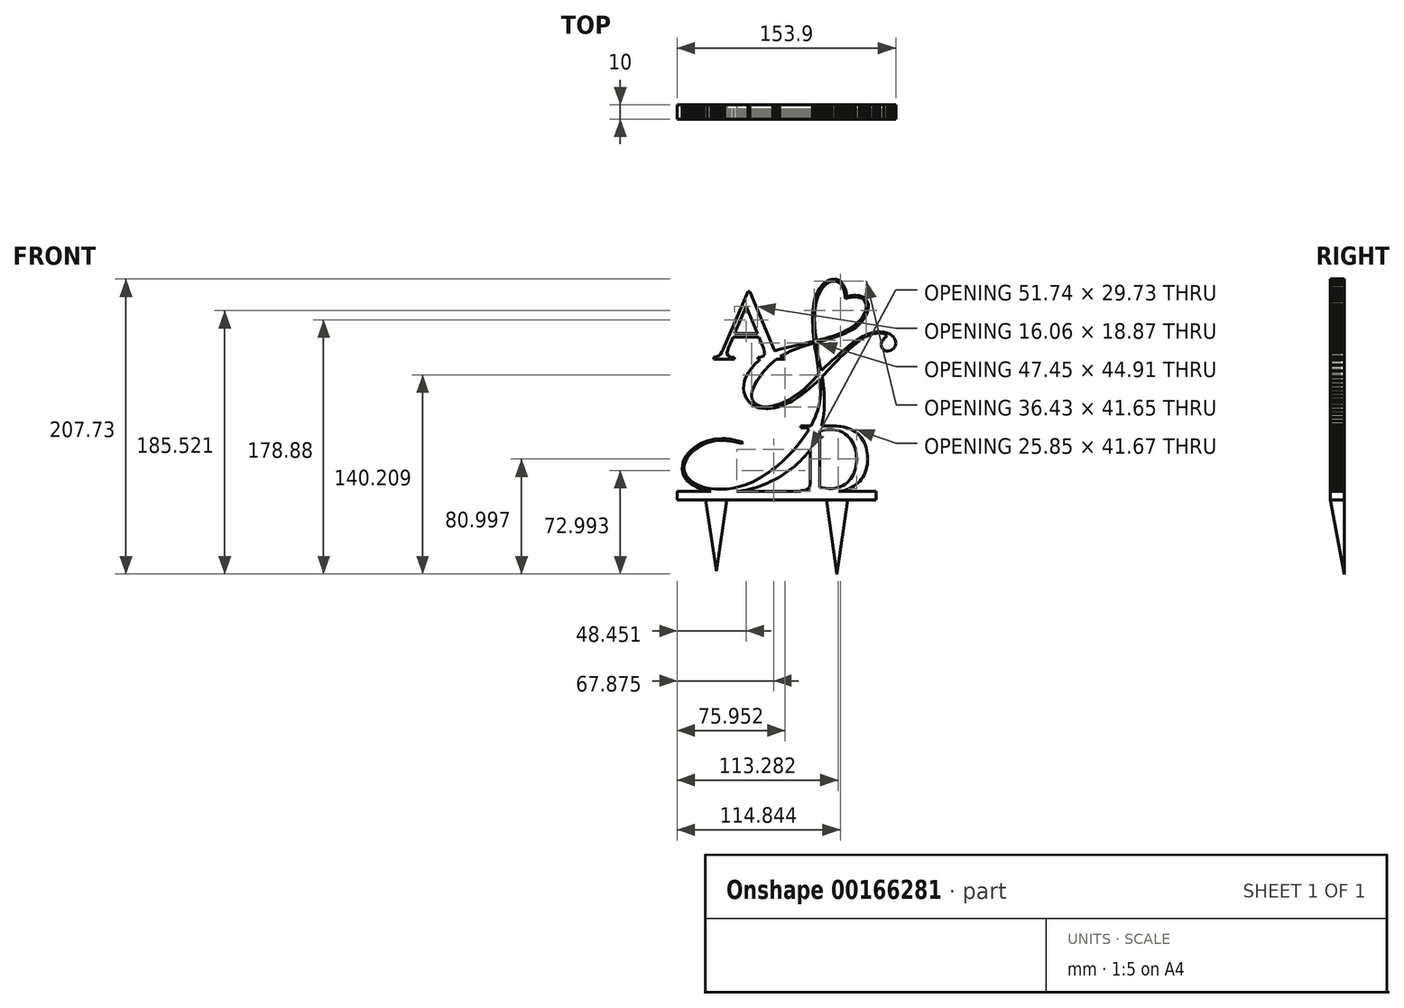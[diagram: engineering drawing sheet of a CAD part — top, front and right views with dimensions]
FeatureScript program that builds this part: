
annotation { "Feature Type Name" : "Feature", "Feature Type Description" : "" }
export const myFeature = defineFeature(function(context is Context, id is Id, definition is map)
    precondition{}
    {
        {
            var Q0;
            Q0=qCreatedBy(makeId("Front.planeOp"),FACE);
            var sketch = newSketch(context, id + "F0", { "sketchPlane" : qUnion([Q0])});
            skLineSegment(sketch, "E0", {"start": v(-55.06, -38.2) * mm, "end": v(-57.57, -38.87) * mm});
            skLineSegment(sketch, "E1", {"start": v(-57.57, -38.87) * mm, "end": v(-59.98, -39.75) * mm});
            skLineSegment(sketch, "E2", {"start": v(-59.98, -39.75) * mm, "end": v(-62.3, -40.8) * mm});
            skLineSegment(sketch, "E3", {"start": v(-62.3, -40.8) * mm, "end": v(-64.52, -42.07) * mm});
            skLineSegment(sketch, "E4", {"start": v(-64.52, -42.07) * mm, "end": v(-66.62, -43.52) * mm});
            skLineSegment(sketch, "E5", {"start": v(-66.62, -43.52) * mm, "end": v(-66.66, -43.54) * mm});
            skLineSegment(sketch, "E6", {"start": v(-66.66, -43.54) * mm, "end": v(-68.92, -45.38) * mm});
            skLineSegment(sketch, "E7", {"start": v(-68.92, -45.38) * mm, "end": v(-70.84, -47.32) * mm});
            skLineSegment(sketch, "E8", {"start": v(-70.84, -47.32) * mm, "end": v(-72.4, -49.38) * mm});
            skLineSegment(sketch, "E9", {"start": v(-72.4, -49.38) * mm, "end": v(-73.63, -51.52) * mm});
            skLineSegment(sketch, "E10", {"start": v(-73.63, -51.52) * mm, "end": v(-74.5, -53.78) * mm});
            skLineSegment(sketch, "E11", {"start": v(-74.5, -53.78) * mm, "end": v(-75.02, -56.15) * mm});
            skLineSegment(sketch, "E12", {"start": v(-75.02, -56.15) * mm, "end": v(-75.2, -58.6) * mm});
            skLineSegment(sketch, "E13", {"start": v(-75.2, -58.6) * mm, "end": v(-75, -60.71) * mm});
            skLineSegment(sketch, "E14", {"start": v(-75, -60.71) * mm, "end": v(-74.34, -62.91) * mm});
            skLineSegment(sketch, "E15", {"start": v(-74.34, -62.91) * mm, "end": v(-73.21, -64.97) * mm});
            skLineSegment(sketch, "E16", {"start": v(-73.21, -64.97) * mm, "end": v(-71.61, -66.9) * mm});
            skLineSegment(sketch, "E17", {"start": v(-71.61, -66.9) * mm, "end": v(-69.54, -68.71) * mm});
            skLineSegment(sketch, "E18", {"start": v(-69.54, -68.71) * mm, "end": v(-67, -70.37) * mm});
            skLineSegment(sketch, "E19", {"start": v(-67, -70.37) * mm, "end": v(-65.02, -71.44) * mm});
            skLineSegment(sketch, "E20", {"start": v(-65.02, -71.44) * mm, "end": v(-62.8, -72.42) * mm});
            skLineSegment(sketch, "E21", {"start": v(-62.8, -72.42) * mm, "end": v(-60.47, -73.23) * mm});
            skLineSegment(sketch, "E22", {"start": v(-60.47, -73.23) * mm, "end": v(-48.47, -72.93) * mm});
            skLineSegment(sketch, "E23", {"start": v(-48.47, -72.93) * mm, "end": v(-49.11, -72.93) * mm});
            skLineSegment(sketch, "E24", {"start": v(-49.11, -72.93) * mm, "end": v(-52.09, -72.82) * mm});
            skLineSegment(sketch, "E25", {"start": v(-52.09, -72.82) * mm, "end": v(-54.91, -72.54) * mm});
            skLineSegment(sketch, "E26", {"start": v(-54.91, -72.54) * mm, "end": v(-57.59, -72.08) * mm});
            skLineSegment(sketch, "E27", {"start": v(-57.59, -72.08) * mm, "end": v(-60.1, -71.46) * mm});
            skLineSegment(sketch, "E28", {"start": v(-60.1, -71.46) * mm, "end": v(-62.48, -70.67) * mm});
            skLineSegment(sketch, "E29", {"start": v(-62.48, -70.67) * mm, "end": v(-64.69, -69.71) * mm});
            skLineSegment(sketch, "E30", {"start": v(-64.69, -69.71) * mm, "end": v(-66.76, -68.58) * mm});
            skLineSegment(sketch, "E31", {"start": v(-66.76, -68.58) * mm, "end": v(-67.19, -68.32) * mm});
            skLineSegment(sketch, "E32", {"start": v(-67.19, -68.32) * mm, "end": v(-69.62, -66.55) * mm});
            skLineSegment(sketch, "E33", {"start": v(-69.62, -66.55) * mm, "end": v(-71.5, -64.65) * mm});
            skLineSegment(sketch, "E34", {"start": v(-71.5, -64.65) * mm, "end": v(-72.84, -62.63) * mm});
            skLineSegment(sketch, "E35", {"start": v(-72.84, -62.63) * mm, "end": v(-73.65, -60.5) * mm});
            skLineSegment(sketch, "E36", {"start": v(-73.65, -60.5) * mm, "end": v(-73.91, -58.23) * mm});
            skLineSegment(sketch, "E37", {"start": v(-73.91, -58.23) * mm, "end": v(-73.9, -57.47) * mm});
            skLineSegment(sketch, "E38", {"start": v(-73.9, -57.47) * mm, "end": v(-73.55, -55.21) * mm});
            skLineSegment(sketch, "E39", {"start": v(-73.55, -55.21) * mm, "end": v(-72.82, -53) * mm});
            skLineSegment(sketch, "E40", {"start": v(-72.82, -53) * mm, "end": v(-71.69, -50.84) * mm});
            skLineSegment(sketch, "E41", {"start": v(-71.69, -50.84) * mm, "end": v(-70.15, -48.74) * mm});
            skLineSegment(sketch, "E42", {"start": v(-70.15, -48.74) * mm, "end": v(-68.2, -46.66) * mm});
            skLineSegment(sketch, "E43", {"start": v(-68.2, -46.66) * mm, "end": v(-65.85, -44.67) * mm});
            skLineSegment(sketch, "E44", {"start": v(-65.85, -44.67) * mm, "end": v(-64.23, -43.52) * mm});
            skLineSegment(sketch, "E45", {"start": v(-64.23, -43.52) * mm, "end": v(-62.05, -42.18) * mm});
            skLineSegment(sketch, "E46", {"start": v(-62.05, -42.18) * mm, "end": v(-59.75, -41.07) * mm});
            skLineSegment(sketch, "E47", {"start": v(-59.75, -41.07) * mm, "end": v(-57.36, -40.15) * mm});
            skLineSegment(sketch, "E48", {"start": v(-57.36, -40.15) * mm, "end": v(-54.86, -39.43) * mm});
            skLineSegment(sketch, "E49", {"start": v(-54.86, -39.43) * mm, "end": v(-52.28, -38.93) * mm});
            skLineSegment(sketch, "E50", {"start": v(-52.28, -38.93) * mm, "end": v(-49.58, -38.63) * mm});
            skLineSegment(sketch, "E51", {"start": v(-49.58, -38.63) * mm, "end": v(-46.8, -38.53) * mm});
            skLineSegment(sketch, "E52", {"start": v(-46.8, -38.53) * mm, "end": v(-55.06, -38.2) * mm});
            skLineSegment(sketch, "E53", {"start": v(-46.55, -37.25) * mm, "end": v(-46.97, -37.25) * mm});
            skLineSegment(sketch, "E54", {"start": v(-46.97, -37.25) * mm, "end": v(-49.77, -37.38) * mm});
            skLineSegment(sketch, "E55", {"start": v(-49.77, -37.38) * mm, "end": v(-52.47, -37.68) * mm});
            skLineSegment(sketch, "E56", {"start": v(-52.47, -37.68) * mm, "end": v(-55.06, -38.2) * mm});
            skLineSegment(sketch, "E57", {"start": v(-55.06, -38.2) * mm, "end": v(-46.8, -38.53) * mm});
            skLineSegment(sketch, "E58", {"start": v(-46.8, -38.53) * mm, "end": v(-46.04, -38.53) * mm});
            skLineSegment(sketch, "E59", {"start": v(-46.04, -38.53) * mm, "end": v(-43.6, -38.66) * mm});
            skLineSegment(sketch, "E60", {"start": v(-43.6, -38.66) * mm, "end": v(-41.07, -38.96) * mm});
            skLineSegment(sketch, "E61", {"start": v(-41.07, -38.96) * mm, "end": v(-38.44, -39.43) * mm});
            skLineSegment(sketch, "E62", {"start": v(-38.44, -39.43) * mm, "end": v(-35.7, -40.06) * mm});
            skLineSegment(sketch, "E63", {"start": v(-35.7, -40.06) * mm, "end": v(-32.87, -40.83) * mm});
            skLineSegment(sketch, "E64", {"start": v(-32.87, -40.83) * mm, "end": v(-32.49, -39.94) * mm});
            skLineSegment(sketch, "E65", {"start": v(-32.49, -39.94) * mm, "end": v(-33.6, -39.55) * mm});
            skLineSegment(sketch, "E66", {"start": v(-33.6, -39.55) * mm, "end": v(-36.25, -38.72) * mm});
            skLineSegment(sketch, "E67", {"start": v(-36.25, -38.72) * mm, "end": v(-38.9, -38.08) * mm});
            skLineSegment(sketch, "E68", {"start": v(-38.9, -38.08) * mm, "end": v(-41.47, -37.6) * mm});
            skLineSegment(sketch, "E69", {"start": v(-41.47, -37.6) * mm, "end": v(-44.03, -37.34) * mm});
            skLineSegment(sketch, "E70", {"start": v(-44.03, -37.34) * mm, "end": v(-46.55, -37.25) * mm});
            skLineSegment(sketch, "E71", {"start": v(17.95, 5.17) * mm, "end": v(16.13, 3.12) * mm});
            skLineSegment(sketch, "E72", {"start": v(16.13, 3.12) * mm, "end": v(14.24, 1.14) * mm});
            skLineSegment(sketch, "E73", {"start": v(14.24, 1.14) * mm, "end": v(12.34, -0.72) * mm});
            skLineSegment(sketch, "E74", {"start": v(12.34, -0.72) * mm, "end": v(10.38, -2.47) * mm});
            skLineSegment(sketch, "E75", {"start": v(10.38, -2.47) * mm, "end": v(8.39, -4.13) * mm});
            skLineSegment(sketch, "E76", {"start": v(8.39, -4.13) * mm, "end": v(6.35, -5.68) * mm});
            skLineSegment(sketch, "E77", {"start": v(6.35, -5.68) * mm, "end": v(4.28, -7.13) * mm});
            skLineSegment(sketch, "E78", {"start": v(4.28, -7.13) * mm, "end": v(2.17, -8.46) * mm});
            skLineSegment(sketch, "E79", {"start": v(2.17, -8.46) * mm, "end": v(0.5, -9.46) * mm});
            skLineSegment(sketch, "E80", {"start": v(0.5, -9.46) * mm, "end": v(-2.14, -10.9) * mm});
            skLineSegment(sketch, "E81", {"start": v(-2.14, -10.9) * mm, "end": v(-4.72, -12.11) * mm});
            skLineSegment(sketch, "E82", {"start": v(-4.72, -12.11) * mm, "end": v(-7.24, -13.1) * mm});
            skLineSegment(sketch, "E83", {"start": v(-7.24, -13.1) * mm, "end": v(-9.69, -13.87) * mm});
            skLineSegment(sketch, "E84", {"start": v(-9.69, -13.87) * mm, "end": v(-12.06, -14.43) * mm});
            skLineSegment(sketch, "E85", {"start": v(-12.06, -14.43) * mm, "end": v(-14.38, -14.75) * mm});
            skLineSegment(sketch, "E86", {"start": v(-14.38, -14.75) * mm, "end": v(-16.63, -14.86) * mm});
            skLineSegment(sketch, "E87", {"start": v(-16.63, -14.86) * mm, "end": v(-7.65, -15.03) * mm});
            skLineSegment(sketch, "E88", {"start": v(-7.65, -15.03) * mm, "end": v(-5.11, -14.22) * mm});
            skLineSegment(sketch, "E89", {"start": v(-5.11, -14.22) * mm, "end": v(-2.51, -13.19) * mm});
            skLineSegment(sketch, "E90", {"start": v(-2.51, -13.19) * mm, "end": v(0.12, -11.93) * mm});
            skLineSegment(sketch, "E91", {"start": v(0.12, -11.93) * mm, "end": v(0.61, -11.68) * mm});
            skLineSegment(sketch, "E92", {"start": v(0.61, -11.68) * mm, "end": v(2.29, -10.76) * mm});
            skLineSegment(sketch, "E93", {"start": v(2.29, -10.76) * mm, "end": v(4.06, -9.67) * mm});
            skLineSegment(sketch, "E94", {"start": v(4.06, -9.67) * mm, "end": v(5.92, -8.42) * mm});
            skLineSegment(sketch, "E95", {"start": v(5.92, -8.42) * mm, "end": v(7.9, -7.03) * mm});
            skLineSegment(sketch, "E96", {"start": v(7.9, -7.03) * mm, "end": v(9.97, -5.47) * mm});
            skLineSegment(sketch, "E97", {"start": v(9.97, -5.47) * mm, "end": v(12.15, -3.75) * mm});
            skLineSegment(sketch, "E98", {"start": v(12.15, -3.75) * mm, "end": v(14.43, -1.87) * mm});
            skLineSegment(sketch, "E99", {"start": v(14.43, -1.87) * mm, "end": v(16.8, 0.16) * mm});
            skLineSegment(sketch, "E100", {"start": v(16.8, 0.16) * mm, "end": v(19.29, 2.35) * mm});
            skLineSegment(sketch, "E101", {"start": v(19.29, 2.35) * mm, "end": v(21.87, 4.7) * mm});
            skLineSegment(sketch, "E102", {"start": v(21.87, 4.7) * mm, "end": v(17.95, 5.17) * mm});
            skLineSegment(sketch, "E103", {"start": v(19.69, 30.42) * mm, "end": v(17.9, 30.04) * mm});
            skLineSegment(sketch, "E104", {"start": v(17.9, 30.04) * mm, "end": v(18.03, 27.09) * mm});
            skLineSegment(sketch, "E105", {"start": v(18.03, 27.09) * mm, "end": v(18.18, 26.52) * mm});
            skLineSegment(sketch, "E106", {"start": v(18.18, 26.52) * mm, "end": v(18.63, 24.24) * mm});
            skLineSegment(sketch, "E107", {"start": v(18.63, 24.24) * mm, "end": v(19.3, 20.3) * mm});
            skLineSegment(sketch, "E108", {"start": v(19.3, 20.3) * mm, "end": v(20.97, 8.94) * mm});
            skLineSegment(sketch, "E109", {"start": v(20.97, 8.94) * mm, "end": v(19.74, 7.35) * mm});
            skLineSegment(sketch, "E110", {"start": v(19.74, 7.35) * mm, "end": v(17.95, 5.17) * mm});
            skLineSegment(sketch, "E111", {"start": v(17.95, 5.17) * mm, "end": v(21.87, 4.7) * mm});
            skLineSegment(sketch, "E112", {"start": v(21.87, 4.7) * mm, "end": v(22.1, 2.57) * mm});
            skLineSegment(sketch, "E113", {"start": v(22.1, 2.57) * mm, "end": v(22.3, -0.16) * mm});
            skLineSegment(sketch, "E114", {"start": v(22.3, -0.16) * mm, "end": v(22.38, -2.46) * mm});
            skLineSegment(sketch, "E115", {"start": v(22.38, -2.46) * mm, "end": v(22.34, -4.06) * mm});
            skLineSegment(sketch, "E116", {"start": v(22.34, -4.06) * mm, "end": v(22.23, -6.35) * mm});
            skLineSegment(sketch, "E117", {"start": v(22.23, -6.35) * mm, "end": v(21.98, -8.65) * mm});
            skLineSegment(sketch, "E118", {"start": v(21.98, -8.65) * mm, "end": v(21.62, -10.93) * mm});
            skLineSegment(sketch, "E119", {"start": v(21.62, -10.93) * mm, "end": v(21.17, -13.23) * mm});
            skLineSegment(sketch, "E120", {"start": v(21.17, -13.23) * mm, "end": v(20.6, -15.5) * mm});
            skLineSegment(sketch, "E121", {"start": v(20.6, -15.5) * mm, "end": v(19.93, -17.8) * mm});
            skLineSegment(sketch, "E122", {"start": v(19.93, -17.8) * mm, "end": v(19.16, -20.08) * mm});
            skLineSegment(sketch, "E123", {"start": v(19.16, -20.08) * mm, "end": v(18.27, -22.36) * mm});
            skLineSegment(sketch, "E124", {"start": v(18.27, -22.36) * mm, "end": v(17.28, -24.64) * mm});
            skLineSegment(sketch, "E125", {"start": v(17.28, -24.64) * mm, "end": v(16.16, -26.91) * mm});
            skLineSegment(sketch, "E126", {"start": v(16.16, -26.91) * mm, "end": v(14.94, -29.2) * mm});
            skLineSegment(sketch, "E127", {"start": v(14.94, -29.2) * mm, "end": v(13.62, -31.45) * mm});
            skLineSegment(sketch, "E128", {"start": v(13.62, -31.45) * mm, "end": v(12.2, -33.73) * mm});
            skLineSegment(sketch, "E129", {"start": v(12.2, -33.73) * mm, "end": v(10.65, -35.99) * mm});
            skLineSegment(sketch, "E130", {"start": v(10.65, -35.99) * mm, "end": v(9, -38.25) * mm});
            skLineSegment(sketch, "E131", {"start": v(9, -38.25) * mm, "end": v(7.22, -40.5) * mm});
            skLineSegment(sketch, "E132", {"start": v(7.22, -40.5) * mm, "end": v(5.36, -42.77) * mm});
            skLineSegment(sketch, "E133", {"start": v(5.36, -42.77) * mm, "end": v(3.38, -45.03) * mm});
            skLineSegment(sketch, "E134", {"start": v(3.38, -45.03) * mm, "end": v(1.29, -47.29) * mm});
            skLineSegment(sketch, "E135", {"start": v(1.29, -47.29) * mm, "end": v(-0.9, -49.53) * mm});
            skLineSegment(sketch, "E136", {"start": v(-0.9, -49.53) * mm, "end": v(-2.9, -51.5) * mm});
            skLineSegment(sketch, "E137", {"start": v(-2.9, -51.5) * mm, "end": v(-5.17, -53.6) * mm});
            skLineSegment(sketch, "E138", {"start": v(-5.17, -53.6) * mm, "end": v(-7.4, -55.57) * mm});
            skLineSegment(sketch, "E139", {"start": v(-7.4, -55.57) * mm, "end": v(-9.67, -57.45) * mm});
            skLineSegment(sketch, "E140", {"start": v(-9.67, -57.45) * mm, "end": v(-11.9, -59.22) * mm});
            skLineSegment(sketch, "E141", {"start": v(-11.9, -59.22) * mm, "end": v(-14.17, -60.88) * mm});
            skLineSegment(sketch, "E142", {"start": v(-14.17, -60.88) * mm, "end": v(-16.43, -62.42) * mm});
            skLineSegment(sketch, "E143", {"start": v(-16.43, -62.42) * mm, "end": v(-18.7, -63.87) * mm});
            skLineSegment(sketch, "E144", {"start": v(-18.7, -63.87) * mm, "end": v(-20.97, -65.21) * mm});
            skLineSegment(sketch, "E145", {"start": v(-20.97, -65.21) * mm, "end": v(-23.24, -66.45) * mm});
            skLineSegment(sketch, "E146", {"start": v(-23.24, -66.45) * mm, "end": v(-25.52, -67.58) * mm});
            skLineSegment(sketch, "E147", {"start": v(-25.52, -67.58) * mm, "end": v(-27.8, -68.6) * mm});
            skLineSegment(sketch, "E148", {"start": v(-27.8, -68.6) * mm, "end": v(-30.08, -69.5) * mm});
            skLineSegment(sketch, "E149", {"start": v(-30.08, -69.5) * mm, "end": v(-32.36, -70.31) * mm});
            skLineSegment(sketch, "E150", {"start": v(-32.36, -70.31) * mm, "end": v(-34.65, -71) * mm});
            skLineSegment(sketch, "E151", {"start": v(-34.65, -71) * mm, "end": v(-36.95, -71.6) * mm});
            skLineSegment(sketch, "E152", {"start": v(-36.95, -71.6) * mm, "end": v(-39.25, -72.08) * mm});
            skLineSegment(sketch, "E153", {"start": v(-39.25, -72.08) * mm, "end": v(-41.54, -72.46) * mm});
            skLineSegment(sketch, "E154", {"start": v(-41.54, -72.46) * mm, "end": v(-43.84, -72.72) * mm});
            skLineSegment(sketch, "E155", {"start": v(-43.84, -72.72) * mm, "end": v(-46.16, -72.87) * mm});
            skLineSegment(sketch, "E156", {"start": v(-46.16, -72.87) * mm, "end": v(-48.47, -72.93) * mm});
            skLineSegment(sketch, "E157", {"start": v(-48.47, -72.93) * mm, "end": v(-60.47, -73.23) * mm});
            skLineSegment(sketch, "E158", {"start": v(-60.47, -73.23) * mm, "end": v(-58, -73.9) * mm});
            skLineSegment(sketch, "E159", {"start": v(-58, -73.9) * mm, "end": v(-55.38, -74.44) * mm});
            skLineSegment(sketch, "E160", {"start": v(-55.38, -74.44) * mm, "end": v(-52.65, -74.81) * mm});
            skLineSegment(sketch, "E161", {"start": v(-52.65, -74.81) * mm, "end": v(-49.8, -75.04) * mm});
            skLineSegment(sketch, "E162", {"start": v(-49.8, -75.04) * mm, "end": v(-46.8, -75.11) * mm});
            skLineSegment(sketch, "E163", {"start": v(-46.8, -75.11) * mm, "end": v(-45.56, -75.1) * mm});
            skLineSegment(sketch, "E164", {"start": v(-45.56, -75.1) * mm, "end": v(-42.9, -75.02) * mm});
            skLineSegment(sketch, "E165", {"start": v(-42.9, -75.02) * mm, "end": v(-40.26, -74.85) * mm});
            skLineSegment(sketch, "E166", {"start": v(-40.26, -74.85) * mm, "end": v(-37.65, -74.6) * mm});
            skLineSegment(sketch, "E167", {"start": v(-37.65, -74.6) * mm, "end": v(-35.07, -74.29) * mm});
            skLineSegment(sketch, "E168", {"start": v(-35.07, -74.29) * mm, "end": v(-32.5, -73.85) * mm});
            skLineSegment(sketch, "E169", {"start": v(-32.5, -73.85) * mm, "end": v(-29.97, -73.36) * mm});
            skLineSegment(sketch, "E170", {"start": v(-29.97, -73.36) * mm, "end": v(-27.46, -72.78) * mm});
            skLineSegment(sketch, "E171", {"start": v(-27.46, -72.78) * mm, "end": v(-24.98, -72.12) * mm});
            skLineSegment(sketch, "E172", {"start": v(-24.98, -72.12) * mm, "end": v(-22.53, -71.37) * mm});
            skLineSegment(sketch, "E173", {"start": v(-22.53, -71.37) * mm, "end": v(-20.1, -70.52) * mm});
            skLineSegment(sketch, "E174", {"start": v(-20.1, -70.52) * mm, "end": v(-17.69, -69.62) * mm});
            skLineSegment(sketch, "E175", {"start": v(-17.69, -69.62) * mm, "end": v(-15.32, -68.62) * mm});
            skLineSegment(sketch, "E176", {"start": v(-15.32, -68.62) * mm, "end": v(-12.94, -67.53) * mm});
            skLineSegment(sketch, "E177", {"start": v(-12.94, -67.53) * mm, "end": v(-10.63, -66.36) * mm});
            skLineSegment(sketch, "E178", {"start": v(-10.63, -66.36) * mm, "end": v(-8.31, -65.1) * mm});
            skLineSegment(sketch, "E179", {"start": v(-8.31, -65.1) * mm, "end": v(-6.05, -63.76) * mm});
            skLineSegment(sketch, "E180", {"start": v(-6.05, -63.76) * mm, "end": v(-3.8, -62.35) * mm});
            skLineSegment(sketch, "E181", {"start": v(-3.8, -62.35) * mm, "end": v(-1.57, -60.84) * mm});
            skLineSegment(sketch, "E182", {"start": v(-1.57, -60.84) * mm, "end": v(0.63, -59.26) * mm});
            skLineSegment(sketch, "E183", {"start": v(0.63, -59.26) * mm, "end": v(2.81, -57.59) * mm});
            skLineSegment(sketch, "E184", {"start": v(2.81, -57.59) * mm, "end": v(3.83, -56.76) * mm});
            skLineSegment(sketch, "E185", {"start": v(3.83, -56.76) * mm, "end": v(5.88, -55) * mm});
            skLineSegment(sketch, "E186", {"start": v(5.88, -55) * mm, "end": v(7.84, -53.18) * mm});
            skLineSegment(sketch, "E187", {"start": v(7.84, -53.18) * mm, "end": v(9.69, -51.32) * mm});
            skLineSegment(sketch, "E188", {"start": v(9.69, -51.32) * mm, "end": v(11.44, -49.4) * mm});
            skLineSegment(sketch, "E189", {"start": v(11.44, -49.4) * mm, "end": v(13.06, -47.44) * mm});
            skLineSegment(sketch, "E190", {"start": v(13.06, -47.44) * mm, "end": v(14.6, -45.4) * mm});
            skLineSegment(sketch, "E191", {"start": v(14.6, -45.4) * mm, "end": v(16.01, -43.33) * mm});
            skLineSegment(sketch, "E192", {"start": v(16.01, -43.33) * mm, "end": v(17.33, -41.2) * mm});
            skLineSegment(sketch, "E193", {"start": v(17.33, -41.2) * mm, "end": v(18.56, -39.04) * mm});
            skLineSegment(sketch, "E194", {"start": v(18.56, -39.04) * mm, "end": v(19.67, -36.8) * mm});
            skLineSegment(sketch, "E195", {"start": v(19.67, -36.8) * mm, "end": v(20.66, -34.52) * mm});
            skLineSegment(sketch, "E196", {"start": v(20.66, -34.52) * mm, "end": v(21.55, -32.19) * mm});
            skLineSegment(sketch, "E197", {"start": v(21.55, -32.19) * mm, "end": v(22.34, -29.81) * mm});
            skLineSegment(sketch, "E198", {"start": v(22.34, -29.81) * mm, "end": v(23.04, -27.37) * mm});
            skLineSegment(sketch, "E199", {"start": v(23.04, -27.37) * mm, "end": v(23.62, -24.88) * mm});
            skLineSegment(sketch, "E200", {"start": v(23.62, -24.88) * mm, "end": v(24.1, -22.34) * mm});
            skLineSegment(sketch, "E201", {"start": v(24.1, -22.34) * mm, "end": v(24.45, -19.76) * mm});
            skLineSegment(sketch, "E202", {"start": v(24.45, -19.76) * mm, "end": v(24.71, -17.1) * mm});
            skLineSegment(sketch, "E203", {"start": v(24.71, -17.1) * mm, "end": v(24.88, -14.41) * mm});
            skLineSegment(sketch, "E204", {"start": v(24.88, -14.41) * mm, "end": v(24.94, -11.66) * mm});
            skLineSegment(sketch, "E205", {"start": v(24.94, -11.66) * mm, "end": v(24.9, -9.87) * mm});
            skLineSegment(sketch, "E206", {"start": v(24.9, -9.87) * mm, "end": v(24.83, -7.48) * mm});
            skLineSegment(sketch, "E207", {"start": v(24.83, -7.48) * mm, "end": v(24.66, -4.96) * mm});
            skLineSegment(sketch, "E208", {"start": v(24.66, -4.96) * mm, "end": v(24.41, -2.32) * mm});
            skLineSegment(sketch, "E209", {"start": v(24.41, -2.32) * mm, "end": v(24.1, 0.44) * mm});
            skLineSegment(sketch, "E210", {"start": v(24.1, 0.44) * mm, "end": v(23.71, 3.34) * mm});
            skLineSegment(sketch, "E211", {"start": v(23.71, 3.34) * mm, "end": v(23.26, 6.37) * mm});
            skLineSegment(sketch, "E212", {"start": v(23.26, 6.37) * mm, "end": v(24.96, 8.26) * mm});
            skLineSegment(sketch, "E213", {"start": v(24.96, 8.26) * mm, "end": v(26.9, 10.4) * mm});
            skLineSegment(sketch, "E214", {"start": v(26.9, 10.4) * mm, "end": v(22.75, 10.6) * mm});
            skLineSegment(sketch, "E215", {"start": v(22.75, 10.6) * mm, "end": v(22.4, 12.08) * mm});
            skLineSegment(sketch, "E216", {"start": v(22.4, 12.08) * mm, "end": v(21.76, 14.85) * mm});
            skLineSegment(sketch, "E217", {"start": v(21.76, 14.85) * mm, "end": v(21.21, 17.58) * mm});
            skLineSegment(sketch, "E218", {"start": v(21.21, 17.58) * mm, "end": v(20.74, 20.23) * mm});
            skLineSegment(sketch, "E219", {"start": v(20.74, 20.23) * mm, "end": v(20.36, 22.85) * mm});
            skLineSegment(sketch, "E220", {"start": v(20.36, 22.85) * mm, "end": v(20.06, 25.43) * mm});
            skLineSegment(sketch, "E221", {"start": v(20.06, 25.43) * mm, "end": v(19.84, 27.95) * mm});
            skLineSegment(sketch, "E222", {"start": v(19.84, 27.95) * mm, "end": v(19.69, 30.42) * mm});
            skLineSegment(sketch, "E223", {"start": v(69.19, 37.2) * mm, "end": v(63.8, 37.07) * mm});
            skLineSegment(sketch, "E224", {"start": v(63.8, 37.07) * mm, "end": v(64.6, 37.03) * mm});
            skLineSegment(sketch, "E225", {"start": v(64.6, 37.03) * mm, "end": v(67.26, 36.43) * mm});
            skLineSegment(sketch, "E226", {"start": v(67.26, 36.43) * mm, "end": v(69.05, 35.14) * mm});
            skLineSegment(sketch, "E227", {"start": v(69.05, 35.14) * mm, "end": v(69.03, 35.05) * mm});
            skLineSegment(sketch, "E228", {"start": v(69.03, 35.05) * mm, "end": v(67.96, 34.19) * mm});
            skLineSegment(sketch, "E229", {"start": v(67.96, 34.19) * mm, "end": v(67, 33.22) * mm});
            skLineSegment(sketch, "E230", {"start": v(67, 33.22) * mm, "end": v(66.25, 32.44) * mm});
            skLineSegment(sketch, "E231", {"start": v(66.25, 32.44) * mm, "end": v(65.64, 31.58) * mm});
            skLineSegment(sketch, "E232", {"start": v(65.64, 31.58) * mm, "end": v(65.14, 30.44) * mm});
            skLineSegment(sketch, "E233", {"start": v(65.14, 30.44) * mm, "end": v(64.84, 29.14) * mm});
            skLineSegment(sketch, "E234", {"start": v(64.84, 29.14) * mm, "end": v(64.97, 27.9) * mm});
            skLineSegment(sketch, "E235", {"start": v(64.97, 27.9) * mm, "end": v(65.46, 26.72) * mm});
            skLineSegment(sketch, "E236", {"start": v(65.46, 26.72) * mm, "end": v(66.23, 25.7) * mm});
            skLineSegment(sketch, "E237", {"start": v(66.23, 25.7) * mm, "end": v(67.11, 24.98) * mm});
            skLineSegment(sketch, "E238", {"start": v(67.11, 24.98) * mm, "end": v(68.3, 24.5) * mm});
            skLineSegment(sketch, "E239", {"start": v(68.3, 24.5) * mm, "end": v(69.56, 24.28) * mm});
            skLineSegment(sketch, "E240", {"start": v(69.56, 24.28) * mm, "end": v(71.16, 24.56) * mm});
            skLineSegment(sketch, "E241", {"start": v(71.16, 24.56) * mm, "end": v(72.4, 25.23) * mm});
            skLineSegment(sketch, "E242", {"start": v(72.4, 25.23) * mm, "end": v(73.4, 26.07) * mm});
            skLineSegment(sketch, "E243", {"start": v(73.4, 26.07) * mm, "end": v(74.55, 27.5) * mm});
            skLineSegment(sketch, "E244", {"start": v(74.55, 27.5) * mm, "end": v(74.97, 28.68) * mm});
            skLineSegment(sketch, "E245", {"start": v(74.97, 28.68) * mm, "end": v(75.2, 29.91) * mm});
            skLineSegment(sketch, "E246", {"start": v(75.2, 29.91) * mm, "end": v(75.04, 31.23) * mm});
            skLineSegment(sketch, "E247", {"start": v(75.04, 31.23) * mm, "end": v(74.58, 32.37) * mm});
            skLineSegment(sketch, "E248", {"start": v(74.58, 32.37) * mm, "end": v(74.04, 33.45) * mm});
            skLineSegment(sketch, "E249", {"start": v(74.04, 33.45) * mm, "end": v(73.23, 34.63) * mm});
            skLineSegment(sketch, "E250", {"start": v(73.23, 34.63) * mm, "end": v(72.12, 35.54) * mm});
            skLineSegment(sketch, "E251", {"start": v(72.12, 35.54) * mm, "end": v(71.37, 36.09) * mm});
            skLineSegment(sketch, "E252", {"start": v(71.37, 36.09) * mm, "end": v(69.19, 37.2) * mm});
            skLineSegment(sketch, "E253", {"start": v(63.8, 38.1) * mm, "end": v(61.67, 37.95) * mm});
            skLineSegment(sketch, "E254", {"start": v(61.67, 37.95) * mm, "end": v(59.38, 37.54) * mm});
            skLineSegment(sketch, "E255", {"start": v(59.38, 37.54) * mm, "end": v(56.97, 36.82) * mm});
            skLineSegment(sketch, "E256", {"start": v(56.97, 36.82) * mm, "end": v(54.46, 35.82) * mm});
            skLineSegment(sketch, "E257", {"start": v(54.46, 35.82) * mm, "end": v(51.83, 34.54) * mm});
            skLineSegment(sketch, "E258", {"start": v(51.83, 34.54) * mm, "end": v(49.1, 32.98) * mm});
            skLineSegment(sketch, "E259", {"start": v(49.1, 32.98) * mm, "end": v(47.78, 32.13) * mm});
            skLineSegment(sketch, "E260", {"start": v(47.78, 32.13) * mm, "end": v(46.3, 31.13) * mm});
            skLineSegment(sketch, "E261", {"start": v(46.3, 31.13) * mm, "end": v(44.73, 29.99) * mm});
            skLineSegment(sketch, "E262", {"start": v(44.73, 29.99) * mm, "end": v(43.03, 28.69) * mm});
            skLineSegment(sketch, "E263", {"start": v(43.03, 28.69) * mm, "end": v(41.22, 27.26) * mm});
            skLineSegment(sketch, "E264", {"start": v(41.22, 27.26) * mm, "end": v(39.32, 25.67) * mm});
            skLineSegment(sketch, "E265", {"start": v(39.32, 25.67) * mm, "end": v(37.29, 23.96) * mm});
            skLineSegment(sketch, "E266", {"start": v(37.29, 23.96) * mm, "end": v(35.14, 22.1) * mm});
            skLineSegment(sketch, "E267", {"start": v(35.14, 22.1) * mm, "end": v(32.9, 20.08) * mm});
            skLineSegment(sketch, "E268", {"start": v(32.9, 20.08) * mm, "end": v(30.53, 17.92) * mm});
            skLineSegment(sketch, "E269", {"start": v(30.53, 17.92) * mm, "end": v(28.04, 15.62) * mm});
            skLineSegment(sketch, "E270", {"start": v(28.04, 15.62) * mm, "end": v(25.47, 13.17) * mm});
            skLineSegment(sketch, "E271", {"start": v(25.47, 13.17) * mm, "end": v(22.75, 10.6) * mm});
            skLineSegment(sketch, "E272", {"start": v(22.75, 10.6) * mm, "end": v(26.9, 10.4) * mm});
            skLineSegment(sketch, "E273", {"start": v(26.9, 10.4) * mm, "end": v(28.82, 12.48) * mm});
            skLineSegment(sketch, "E274", {"start": v(28.82, 12.48) * mm, "end": v(30.72, 14.49) * mm});
            skLineSegment(sketch, "E275", {"start": v(30.72, 14.49) * mm, "end": v(32.6, 16.43) * mm});
            skLineSegment(sketch, "E276", {"start": v(32.6, 16.43) * mm, "end": v(34.47, 18.31) * mm});
            skLineSegment(sketch, "E277", {"start": v(34.47, 18.31) * mm, "end": v(36.3, 20.12) * mm});
            skLineSegment(sketch, "E278", {"start": v(36.3, 20.12) * mm, "end": v(38.12, 21.87) * mm});
            skLineSegment(sketch, "E279", {"start": v(38.12, 21.87) * mm, "end": v(39.9, 23.57) * mm});
            skLineSegment(sketch, "E280", {"start": v(39.9, 23.57) * mm, "end": v(41.68, 25.17) * mm});
            skLineSegment(sketch, "E281", {"start": v(41.68, 25.17) * mm, "end": v(42.2, 25.64) * mm});
            skLineSegment(sketch, "E282", {"start": v(42.2, 25.64) * mm, "end": v(44.86, 27.91) * mm});
            skLineSegment(sketch, "E283", {"start": v(44.86, 27.91) * mm, "end": v(47.3, 29.91) * mm});
            skLineSegment(sketch, "E284", {"start": v(47.3, 29.91) * mm, "end": v(49.53, 31.62) * mm});
            skLineSegment(sketch, "E285", {"start": v(49.53, 31.62) * mm, "end": v(51.52, 33.04) * mm});
            skLineSegment(sketch, "E286", {"start": v(51.52, 33.04) * mm, "end": v(53.3, 34.17) * mm});
            skLineSegment(sketch, "E287", {"start": v(53.3, 34.17) * mm, "end": v(54.86, 35.01) * mm});
            skLineSegment(sketch, "E288", {"start": v(54.86, 35.01) * mm, "end": v(56.08, 35.56) * mm});
            skLineSegment(sketch, "E289", {"start": v(56.08, 35.56) * mm, "end": v(58.62, 36.4) * mm});
            skLineSegment(sketch, "E290", {"start": v(58.62, 36.4) * mm, "end": v(61.18, 36.9) * mm});
            skLineSegment(sketch, "E291", {"start": v(61.18, 36.9) * mm, "end": v(63.8, 37.07) * mm});
            skLineSegment(sketch, "E292", {"start": v(63.8, 37.07) * mm, "end": v(69.19, 37.2) * mm});
            skLineSegment(sketch, "E293", {"start": v(69.19, 37.2) * mm, "end": v(66.66, 37.87) * mm});
            skLineSegment(sketch, "E294", {"start": v(66.66, 37.87) * mm, "end": v(63.8, 38.1) * mm});
            skLineSegment(sketch, "E295", {"start": v(51.8, 62.58) * mm, "end": v(46.16, 62.39) * mm});
            skLineSegment(sketch, "E296", {"start": v(46.16, 62.39) * mm, "end": v(49.06, 62.14) * mm});
            skLineSegment(sketch, "E297", {"start": v(49.06, 62.14) * mm, "end": v(51.37, 61.37) * mm});
            skLineSegment(sketch, "E298", {"start": v(51.37, 61.37) * mm, "end": v(53.01, 60.05) * mm});
            skLineSegment(sketch, "E299", {"start": v(53.01, 60.05) * mm, "end": v(54, 58.23) * mm});
            skLineSegment(sketch, "E300", {"start": v(54, 58.23) * mm, "end": v(54.35, 55.87) * mm});
            skLineSegment(sketch, "E301", {"start": v(54.35, 55.87) * mm, "end": v(54.24, 54.35) * mm});
            skLineSegment(sketch, "E302", {"start": v(54.24, 54.35) * mm, "end": v(53.76, 52.2) * mm});
            skLineSegment(sketch, "E303", {"start": v(53.76, 52.2) * mm, "end": v(52.86, 50.1) * mm});
            skLineSegment(sketch, "E304", {"start": v(52.86, 50.1) * mm, "end": v(51.58, 48) * mm});
            skLineSegment(sketch, "E305", {"start": v(51.58, 48) * mm, "end": v(49.87, 45.95) * mm});
            skLineSegment(sketch, "E306", {"start": v(49.87, 45.95) * mm, "end": v(47.78, 43.94) * mm});
            skLineSegment(sketch, "E307", {"start": v(47.78, 43.94) * mm, "end": v(45.27, 41.92) * mm});
            skLineSegment(sketch, "E308", {"start": v(45.27, 41.92) * mm, "end": v(44.28, 41.25) * mm});
            skLineSegment(sketch, "E309", {"start": v(44.28, 41.25) * mm, "end": v(42.4, 40.04) * mm});
            skLineSegment(sketch, "E310", {"start": v(42.4, 40.04) * mm, "end": v(40.38, 38.91) * mm});
            skLineSegment(sketch, "E311", {"start": v(40.38, 38.91) * mm, "end": v(38.21, 37.84) * mm});
            skLineSegment(sketch, "E312", {"start": v(38.21, 37.84) * mm, "end": v(35.92, 36.84) * mm});
            skLineSegment(sketch, "E313", {"start": v(35.92, 36.84) * mm, "end": v(33.49, 35.88) * mm});
            skLineSegment(sketch, "E314", {"start": v(33.49, 35.88) * mm, "end": v(30.93, 35) * mm});
            skLineSegment(sketch, "E315", {"start": v(30.93, 35) * mm, "end": v(28.21, 34.18) * mm});
            skLineSegment(sketch, "E316", {"start": v(28.21, 34.18) * mm, "end": v(25.4, 33.41) * mm});
            skLineSegment(sketch, "E317", {"start": v(25.4, 33.41) * mm, "end": v(22.42, 32.72) * mm});
            skLineSegment(sketch, "E318", {"start": v(22.42, 32.72) * mm, "end": v(19.3, 32.08) * mm});
            skLineSegment(sketch, "E319", {"start": v(19.3, 32.08) * mm, "end": v(17.9, 31.57) * mm});
            skLineSegment(sketch, "E320", {"start": v(17.9, 31.57) * mm, "end": v(-6.66, 25.56) * mm});
            skLineSegment(sketch, "E321", {"start": v(-6.66, 25.56) * mm, "end": v(-8.54, 25.01) * mm});
            skLineSegment(sketch, "E322", {"start": v(-8.54, 25.01) * mm, "end": v(-10.93, 24.17) * mm});
            skLineSegment(sketch, "E323", {"start": v(-10.93, 24.17) * mm, "end": v(-13.26, 23.13) * mm});
            skLineSegment(sketch, "E324", {"start": v(-13.26, 23.13) * mm, "end": v(-15.54, 21.9) * mm});
            skLineSegment(sketch, "E325", {"start": v(-15.54, 21.9) * mm, "end": v(-17.75, 20.5) * mm});
            skLineSegment(sketch, "E326", {"start": v(-17.75, 20.5) * mm, "end": v(-19.91, 18.91) * mm});
            skLineSegment(sketch, "E327", {"start": v(-19.91, 18.91) * mm, "end": v(-22, 17.14) * mm});
            skLineSegment(sketch, "E328", {"start": v(-22, 17.14) * mm, "end": v(-24.05, 15.19) * mm});
            skLineSegment(sketch, "E329", {"start": v(-24.05, 15.19) * mm, "end": v(-24.88, 14.32) * mm});
            skLineSegment(sketch, "E330", {"start": v(-24.88, 14.32) * mm, "end": v(-26.76, 12.16) * mm});
            skLineSegment(sketch, "E331", {"start": v(-26.76, 12.16) * mm, "end": v(-28.37, 9.93) * mm});
            skLineSegment(sketch, "E332", {"start": v(-28.37, 9.93) * mm, "end": v(-29.66, 7.66) * mm});
            skLineSegment(sketch, "E333", {"start": v(-29.66, 7.66) * mm, "end": v(-30.66, 5.36) * mm});
            skLineSegment(sketch, "E334", {"start": v(-30.66, 5.36) * mm, "end": v(-31.4, 3) * mm});
            skLineSegment(sketch, "E335", {"start": v(-31.4, 3) * mm, "end": v(-31.83, 0.61) * mm});
            skLineSegment(sketch, "E336", {"start": v(-31.83, 0.61) * mm, "end": v(-31.98, -1.82) * mm});
            skLineSegment(sketch, "E337", {"start": v(-31.98, -1.82) * mm, "end": v(-31.96, -2.06) * mm});
            skLineSegment(sketch, "E338", {"start": v(-31.96, -2.06) * mm, "end": v(-31.68, -4.53) * mm});
            skLineSegment(sketch, "E339", {"start": v(-31.68, -4.53) * mm, "end": v(-30.93, -6.92) * mm});
            skLineSegment(sketch, "E340", {"start": v(-30.93, -6.92) * mm, "end": v(-29.7, -9.27) * mm});
            skLineSegment(sketch, "E341", {"start": v(-29.7, -9.27) * mm, "end": v(-28, -11.53) * mm});
            skLineSegment(sketch, "E342", {"start": v(-28, -11.53) * mm, "end": v(-27.52, -12.08) * mm});
            skLineSegment(sketch, "E343", {"start": v(-27.52, -12.08) * mm, "end": v(-25.77, -13.55) * mm});
            skLineSegment(sketch, "E344", {"start": v(-25.77, -13.55) * mm, "end": v(-23.68, -14.68) * mm});
            skLineSegment(sketch, "E345", {"start": v(-23.68, -14.68) * mm, "end": v(-21.27, -15.48) * mm});
            skLineSegment(sketch, "E346", {"start": v(-21.27, -15.48) * mm, "end": v(-18.54, -15.97) * mm});
            skLineSegment(sketch, "E347", {"start": v(-18.54, -15.97) * mm, "end": v(-15.47, -16.14) * mm});
            skLineSegment(sketch, "E348", {"start": v(-15.47, -16.14) * mm, "end": v(-15.1, -16.14) * mm});
            skLineSegment(sketch, "E349", {"start": v(-15.1, -16.14) * mm, "end": v(-12.64, -16) * mm});
            skLineSegment(sketch, "E350", {"start": v(-12.64, -16) * mm, "end": v(-10.18, -15.62) * mm});
            skLineSegment(sketch, "E351", {"start": v(-10.18, -15.62) * mm, "end": v(-7.65, -15.03) * mm});
            skLineSegment(sketch, "E352", {"start": v(-7.65, -15.03) * mm, "end": v(-16.63, -14.86) * mm});
            skLineSegment(sketch, "E353", {"start": v(-16.63, -14.86) * mm, "end": v(-19.3, -14.64) * mm});
            skLineSegment(sketch, "E354", {"start": v(-19.3, -14.64) * mm, "end": v(-21.76, -13.87) * mm});
            skLineSegment(sketch, "E355", {"start": v(-21.76, -13.87) * mm, "end": v(-23.79, -12.57) * mm});
            skLineSegment(sketch, "E356", {"start": v(-23.79, -12.57) * mm, "end": v(-24.75, -11.63) * mm});
            skLineSegment(sketch, "E357", {"start": v(-24.75, -11.63) * mm, "end": v(-26.05, -9.44) * mm});
            skLineSegment(sketch, "E358", {"start": v(-26.05, -9.44) * mm, "end": v(-26.48, -6.94) * mm});
            skLineSegment(sketch, "E359", {"start": v(-26.48, -6.94) * mm, "end": v(-26.39, -5.79) * mm});
            skLineSegment(sketch, "E360", {"start": v(-26.39, -5.79) * mm, "end": v(-25.95, -3.83) * mm});
            skLineSegment(sketch, "E361", {"start": v(-25.95, -3.83) * mm, "end": v(-25.15, -1.63) * mm});
            skLineSegment(sketch, "E362", {"start": v(-25.15, -1.63) * mm, "end": v(-23.96, 0.84) * mm});
            skLineSegment(sketch, "E363", {"start": v(-23.96, 0.84) * mm, "end": v(-22.4, 3.55) * mm});
            skLineSegment(sketch, "E364", {"start": v(-22.4, 3.55) * mm, "end": v(-20.46, 6.49) * mm});
            skLineSegment(sketch, "E365", {"start": v(-20.46, 6.49) * mm, "end": v(-19.76, 7.49) * mm});
            skLineSegment(sketch, "E366", {"start": v(-19.76, 7.49) * mm, "end": v(-18.08, 9.67) * mm});
            skLineSegment(sketch, "E367", {"start": v(-18.08, 9.67) * mm, "end": v(-16.33, 11.74) * mm});
            skLineSegment(sketch, "E368", {"start": v(-16.33, 11.74) * mm, "end": v(-14.5, 13.7) * mm});
            skLineSegment(sketch, "E369", {"start": v(-14.5, 13.7) * mm, "end": v(-12.6, 15.53) * mm});
            skLineSegment(sketch, "E370", {"start": v(-12.6, 15.53) * mm, "end": v(-10.65, 17.24) * mm});
            skLineSegment(sketch, "E371", {"start": v(-10.65, 17.24) * mm, "end": v(-8.63, 18.84) * mm});
            skLineSegment(sketch, "E372", {"start": v(-8.63, 18.84) * mm, "end": v(-6.52, 20.3) * mm});
            skLineSegment(sketch, "E373", {"start": v(-6.52, 20.3) * mm, "end": v(-5.02, 21.25) * mm});
            skLineSegment(sketch, "E374", {"start": v(-5.02, 21.25) * mm, "end": v(-3.2, 22.27) * mm});
            skLineSegment(sketch, "E375", {"start": v(-3.2, 22.27) * mm, "end": v(-1.18, 23.26) * mm});
            skLineSegment(sketch, "E376", {"start": v(-1.18, 23.26) * mm, "end": v(1, 24.26) * mm});
            skLineSegment(sketch, "E377", {"start": v(1, 24.26) * mm, "end": v(3.38, 25.26) * mm});
            skLineSegment(sketch, "E378", {"start": v(3.38, 25.26) * mm, "end": v(5.92, 26.24) * mm});
            skLineSegment(sketch, "E379", {"start": v(5.92, 26.24) * mm, "end": v(8.65, 27.2) * mm});
            skLineSegment(sketch, "E380", {"start": v(8.65, 27.2) * mm, "end": v(11.55, 28.16) * mm});
            skLineSegment(sketch, "E381", {"start": v(11.55, 28.16) * mm, "end": v(14.64, 29.1) * mm});
            skLineSegment(sketch, "E382", {"start": v(14.64, 29.1) * mm, "end": v(17.9, 30.04) * mm});
            skLineSegment(sketch, "E383", {"start": v(17.9, 30.04) * mm, "end": v(19.69, 30.42) * mm});
            skLineSegment(sketch, "E384", {"start": v(19.69, 30.42) * mm, "end": v(23.07, 31.3) * mm});
            skLineSegment(sketch, "E385", {"start": v(23.07, 31.3) * mm, "end": v(26.4, 32.25) * mm});
            skLineSegment(sketch, "E386", {"start": v(26.4, 32.25) * mm, "end": v(29.55, 33.2) * mm});
            skLineSegment(sketch, "E387", {"start": v(29.55, 33.2) * mm, "end": v(32.49, 34.17) * mm});
            skLineSegment(sketch, "E388", {"start": v(32.49, 34.17) * mm, "end": v(35.22, 35.14) * mm});
            skLineSegment(sketch, "E389", {"start": v(35.22, 35.14) * mm, "end": v(37.76, 36.14) * mm});
            skLineSegment(sketch, "E390", {"start": v(37.76, 36.14) * mm, "end": v(40.1, 37.16) * mm});
            skLineSegment(sketch, "E391", {"start": v(40.1, 37.16) * mm, "end": v(42.22, 38.2) * mm});
            skLineSegment(sketch, "E392", {"start": v(42.22, 38.2) * mm, "end": v(44.14, 39.23) * mm});
            skLineSegment(sketch, "E393", {"start": v(44.14, 39.23) * mm, "end": v(45.88, 40.28) * mm});
            skLineSegment(sketch, "E394", {"start": v(45.88, 40.28) * mm, "end": v(47.4, 41.36) * mm});
            skLineSegment(sketch, "E395", {"start": v(47.4, 41.36) * mm, "end": v(48.72, 42.43) * mm});
            skLineSegment(sketch, "E396", {"start": v(48.72, 42.43) * mm, "end": v(50.88, 44.62) * mm});
            skLineSegment(sketch, "E397", {"start": v(50.88, 44.62) * mm, "end": v(52.7, 46.8) * mm});
            skLineSegment(sketch, "E398", {"start": v(52.7, 46.8) * mm, "end": v(54.08, 49.02) * mm});
            skLineSegment(sketch, "E399", {"start": v(54.08, 49.02) * mm, "end": v(55.08, 51.24) * mm});
            skLineSegment(sketch, "E400", {"start": v(55.08, 51.24) * mm, "end": v(55.69, 53.48) * mm});
            skLineSegment(sketch, "E401", {"start": v(55.69, 53.48) * mm, "end": v(55.87, 55.74) * mm});
            skLineSegment(sketch, "E402", {"start": v(55.87, 55.74) * mm, "end": v(55.78, 57.1) * mm});
            skLineSegment(sketch, "E403", {"start": v(55.78, 57.1) * mm, "end": v(55, 59.53) * mm});
            skLineSegment(sketch, "E404", {"start": v(55, 59.53) * mm, "end": v(53.44, 61.5) * mm});
            skLineSegment(sketch, "E405", {"start": v(53.44, 61.5) * mm, "end": v(51.8, 62.58) * mm});
            skLineSegment(sketch, "E406", {"start": v(-27.69, 66.39) * mm, "end": v(-28.9, 66.39) * mm});
            skLineSegment(sketch, "E407", {"start": v(-28.9, 66.39) * mm, "end": v(-45.3, 27.96) * mm});
            skLineSegment(sketch, "E408", {"start": v(-45.3, 27.96) * mm, "end": v(-45.37, 27.77) * mm});
            skLineSegment(sketch, "E409", {"start": v(-45.37, 27.77) * mm, "end": v(-46.4, 25.53) * mm});
            skLineSegment(sketch, "E410", {"start": v(-46.4, 25.53) * mm, "end": v(-47.38, 23.7) * mm});
            skLineSegment(sketch, "E411", {"start": v(-47.38, 23.7) * mm, "end": v(-48.33, 22.27) * mm});
            skLineSegment(sketch, "E412", {"start": v(-48.33, 22.27) * mm, "end": v(-49.2, 21.26) * mm});
            skLineSegment(sketch, "E413", {"start": v(-49.2, 21.26) * mm, "end": v(-49.32, 21.14) * mm});
            skLineSegment(sketch, "E414", {"start": v(-49.32, 21.14) * mm, "end": v(-50.7, 20.46) * mm});
            skLineSegment(sketch, "E415", {"start": v(-50.7, 20.46) * mm, "end": v(-53, 19.92) * mm});
            skLineSegment(sketch, "E416", {"start": v(-53, 19.92) * mm, "end": v(-53, 18.64) * mm});
            skLineSegment(sketch, "E417", {"start": v(-53, 18.64) * mm, "end": v(-38.29, 18.64) * mm});
            skLineSegment(sketch, "E418", {"start": v(-38.29, 18.64) * mm, "end": v(-38.29, 19.92) * mm});
            skLineSegment(sketch, "E419", {"start": v(-38.29, 19.92) * mm, "end": v(-39.34, 20) * mm});
            skLineSegment(sketch, "E420", {"start": v(-39.34, 20) * mm, "end": v(-41.42, 20.33) * mm});
            skLineSegment(sketch, "E421", {"start": v(-41.42, 20.33) * mm, "end": v(-42.66, 20.92) * mm});
            skLineSegment(sketch, "E422", {"start": v(-42.66, 20.92) * mm, "end": v(-42.98, 21.2) * mm});
            skLineSegment(sketch, "E423", {"start": v(-42.98, 21.2) * mm, "end": v(-43.66, 22.84) * mm});
            skLineSegment(sketch, "E424", {"start": v(-43.66, 22.84) * mm, "end": v(-43.66, 23.12) * mm});
            skLineSegment(sketch, "E425", {"start": v(-43.66, 23.12) * mm, "end": v(-43.32, 24.76) * mm});
            skLineSegment(sketch, "E426", {"start": v(-43.32, 24.76) * mm, "end": v(-42.5, 26.87) * mm});
            skLineSegment(sketch, "E427", {"start": v(-42.5, 26.87) * mm, "end": v(-39.34, 34.25) * mm});
            skLineSegment(sketch, "E428", {"start": v(-39.34, 34.25) * mm, "end": v(-21.27, 34.25) * mm});
            skLineSegment(sketch, "E429", {"start": v(-21.27, 34.25) * mm, "end": v(-38.29, 36.83) * mm});
            skLineSegment(sketch, "E430", {"start": v(-38.29, 36.83) * mm, "end": v(-30.14, 55.7) * mm});
            skLineSegment(sketch, "E431", {"start": v(-30.14, 55.7) * mm, "end": v(-27.69, 66.39) * mm});
            skLineSegment(sketch, "E432", {"start": v(-27.69, 66.39) * mm, "end": v(-30.14, 55.7) * mm});
            skLineSegment(sketch, "E433", {"start": v(-30.14, 55.7) * mm, "end": v(-22.23, 36.83) * mm});
            skLineSegment(sketch, "E434", {"start": v(-22.23, 36.83) * mm, "end": v(-38.29, 36.83) * mm});
            skLineSegment(sketch, "E435", {"start": v(-38.29, 36.83) * mm, "end": v(-21.27, 34.25) * mm});
            skLineSegment(sketch, "E436", {"start": v(-21.27, 34.25) * mm, "end": v(-18.44, 27.54) * mm});
            skLineSegment(sketch, "E437", {"start": v(-18.44, 27.54) * mm, "end": v(-17.88, 26.1) * mm});
            skLineSegment(sketch, "E438", {"start": v(-17.88, 26.1) * mm, "end": v(-17.28, 24.17) * mm});
            skLineSegment(sketch, "E439", {"start": v(-17.28, 24.17) * mm, "end": v(-17.07, 22.74) * mm});
            skLineSegment(sketch, "E440", {"start": v(-17.07, 22.74) * mm, "end": v(-17.28, 21.7) * mm});
            skLineSegment(sketch, "E441", {"start": v(-17.28, 21.7) * mm, "end": v(-18.07, 20.84) * mm});
            skLineSegment(sketch, "E442", {"start": v(-18.07, 20.84) * mm, "end": v(-19.52, 20.22) * mm});
            skLineSegment(sketch, "E443", {"start": v(-19.52, 20.22) * mm, "end": v(-19.86, 20.13) * mm});
            skLineSegment(sketch, "E444", {"start": v(-19.86, 20.13) * mm, "end": v(-21.81, 19.92) * mm});
            skLineSegment(sketch, "E445", {"start": v(-21.81, 19.92) * mm, "end": v(-21.81, 18.64) * mm});
            skLineSegment(sketch, "E446", {"start": v(-21.81, 18.64) * mm, "end": v(-3.42, 18.64) * mm});
            skLineSegment(sketch, "E447", {"start": v(-3.42, 18.64) * mm, "end": v(-3.42, 19.92) * mm});
            skLineSegment(sketch, "E448", {"start": v(-3.42, 19.92) * mm, "end": v(-4.59, 20.05) * mm});
            skLineSegment(sketch, "E449", {"start": v(-4.59, 20.05) * mm, "end": v(-6.43, 20.58) * mm});
            skLineSegment(sketch, "E450", {"start": v(-6.43, 20.58) * mm, "end": v(-7.86, 21.46) * mm});
            skLineSegment(sketch, "E451", {"start": v(-7.86, 21.46) * mm, "end": v(-8.5, 22.14) * mm});
            skLineSegment(sketch, "E452", {"start": v(-8.5, 22.14) * mm, "end": v(-9.44, 23.5) * mm});
            skLineSegment(sketch, "E453", {"start": v(-9.44, 23.5) * mm, "end": v(-10.42, 25.3) * mm});
            skLineSegment(sketch, "E454", {"start": v(-10.42, 25.3) * mm, "end": v(-11.44, 27.54) * mm});
            skLineSegment(sketch, "E455", {"start": v(-11.44, 27.54) * mm, "end": v(-27.69, 66.39) * mm});
            skLineSegment(sketch, "E456", {"start": v(43.3, -30.54) * mm, "end": v(28.73, -30.79) * mm});
            skLineSegment(sketch, "E457", {"start": v(28.73, -30.79) * mm, "end": v(28.86, -30.79) * mm});
            skLineSegment(sketch, "E458", {"start": v(28.86, -30.79) * mm, "end": v(30.83, -30.88) * mm});
            skLineSegment(sketch, "E459", {"start": v(30.83, -30.88) * mm, "end": v(32.74, -31.17) * mm});
            skLineSegment(sketch, "E460", {"start": v(32.74, -31.17) * mm, "end": v(34.56, -31.62) * mm});
            skLineSegment(sketch, "E461", {"start": v(34.56, -31.62) * mm, "end": v(36.3, -32.24) * mm});
            skLineSegment(sketch, "E462", {"start": v(36.3, -32.24) * mm, "end": v(37.7, -32.92) * mm});
            skLineSegment(sketch, "E463", {"start": v(37.7, -32.92) * mm, "end": v(39.35, -33.91) * mm});
            skLineSegment(sketch, "E464", {"start": v(39.35, -33.91) * mm, "end": v(40.83, -35.08) * mm});
            skLineSegment(sketch, "E465", {"start": v(40.83, -35.08) * mm, "end": v(42.2, -36.42) * mm});
            skLineSegment(sketch, "E466", {"start": v(42.2, -36.42) * mm, "end": v(42.23, -36.42) * mm});
            skLineSegment(sketch, "E467", {"start": v(42.23, -36.42) * mm, "end": v(43.4, -37.85) * mm});
            skLineSegment(sketch, "E468", {"start": v(43.4, -37.85) * mm, "end": v(44.45, -39.41) * mm});
            skLineSegment(sketch, "E469", {"start": v(44.45, -39.41) * mm, "end": v(45.35, -41.1) * mm});
            skLineSegment(sketch, "E470", {"start": v(45.35, -41.1) * mm, "end": v(46.12, -42.95) * mm});
            skLineSegment(sketch, "E471", {"start": v(46.12, -42.95) * mm, "end": v(46.46, -44) * mm});
            skLineSegment(sketch, "E472", {"start": v(46.46, -44) * mm, "end": v(46.91, -45.78) * mm});
            skLineSegment(sketch, "E473", {"start": v(46.91, -45.78) * mm, "end": v(47.23, -47.64) * mm});
            skLineSegment(sketch, "E474", {"start": v(47.23, -47.64) * mm, "end": v(47.44, -49.6) * mm});
            skLineSegment(sketch, "E475", {"start": v(47.44, -49.6) * mm, "end": v(47.5, -51.65) * mm});
            skLineSegment(sketch, "E476", {"start": v(47.5, -51.65) * mm, "end": v(47.48, -52.84) * mm});
            skLineSegment(sketch, "E477", {"start": v(47.48, -52.84) * mm, "end": v(47.33, -54.83) * mm});
            skLineSegment(sketch, "E478", {"start": v(47.33, -54.83) * mm, "end": v(47.06, -56.73) * mm});
            skLineSegment(sketch, "E479", {"start": v(47.06, -56.73) * mm, "end": v(46.65, -58.54) * mm});
            skLineSegment(sketch, "E480", {"start": v(46.65, -58.54) * mm, "end": v(46.12, -60.27) * mm});
            skLineSegment(sketch, "E481", {"start": v(46.12, -60.27) * mm, "end": v(46.1, -60.3) * mm});
            skLineSegment(sketch, "E482", {"start": v(46.1, -60.3) * mm, "end": v(45.33, -62.16) * mm});
            skLineSegment(sketch, "E483", {"start": v(45.33, -62.16) * mm, "end": v(44.45, -63.85) * mm});
            skLineSegment(sketch, "E484", {"start": v(44.45, -63.85) * mm, "end": v(43.41, -65.41) * mm});
            skLineSegment(sketch, "E485", {"start": v(43.41, -65.41) * mm, "end": v(42.24, -66.85) * mm});
            skLineSegment(sketch, "E486", {"start": v(42.24, -66.85) * mm, "end": v(41.17, -67.92) * mm});
            skLineSegment(sketch, "E487", {"start": v(41.17, -67.92) * mm, "end": v(39.7, -69.12) * mm});
            skLineSegment(sketch, "E488", {"start": v(39.7, -69.12) * mm, "end": v(38.1, -70.16) * mm});
            skLineSegment(sketch, "E489", {"start": v(38.1, -70.16) * mm, "end": v(36.39, -71) * mm});
            skLineSegment(sketch, "E490", {"start": v(36.39, -71) * mm, "end": v(34.68, -71.63) * mm});
            skLineSegment(sketch, "E491", {"start": v(34.68, -71.63) * mm, "end": v(32.85, -72.1) * mm});
            skLineSegment(sketch, "E492", {"start": v(32.85, -72.1) * mm, "end": v(30.95, -72.38) * mm});
            skLineSegment(sketch, "E493", {"start": v(30.95, -72.38) * mm, "end": v(28.97, -72.46) * mm});
            skLineSegment(sketch, "E494", {"start": v(28.97, -72.46) * mm, "end": v(13.6, -72.48) * mm});
            skLineSegment(sketch, "E495", {"start": v(13.6, -72.48) * mm, "end": v(12.1, -73.3) * mm});
            skLineSegment(sketch, "E496", {"start": v(12.1, -73.3) * mm, "end": v(10.09, -73.59) * mm});
            skLineSegment(sketch, "E497", {"start": v(10.09, -73.59) * mm, "end": v(8.33, -73.59) * mm});
            skLineSegment(sketch, "E498", {"start": v(8.33, -73.59) * mm, "end": v(8.33, -74.89) * mm});
            skLineSegment(sketch, "E499", {"start": v(8.33, -74.89) * mm, "end": v(29.18, -74.89) * mm});
            skLineSegment(sketch, "E500", {"start": v(29.18, -74.89) * mm, "end": v(29.3, -74.89) * mm});
            skLineSegment(sketch, "E501", {"start": v(29.3, -74.89) * mm, "end": v(31.4, -74.83) * mm});
            skLineSegment(sketch, "E502", {"start": v(31.4, -74.83) * mm, "end": v(33.41, -74.68) * mm});
            skLineSegment(sketch, "E503", {"start": v(33.41, -74.68) * mm, "end": v(35.33, -74.43) * mm});
            skLineSegment(sketch, "E504", {"start": v(35.33, -74.43) * mm, "end": v(37.16, -74.1) * mm});
            skLineSegment(sketch, "E505", {"start": v(37.16, -74.1) * mm, "end": v(38.91, -73.66) * mm});
            skLineSegment(sketch, "E506", {"start": v(38.91, -73.66) * mm, "end": v(40.59, -73.13) * mm});
            skLineSegment(sketch, "E507", {"start": v(40.59, -73.13) * mm, "end": v(40.63, -73.12) * mm});
            skLineSegment(sketch, "E508", {"start": v(40.63, -73.12) * mm, "end": v(42.5, -72.36) * mm});
            skLineSegment(sketch, "E509", {"start": v(42.5, -72.36) * mm, "end": v(44.26, -71.5) * mm});
            skLineSegment(sketch, "E510", {"start": v(44.26, -71.5) * mm, "end": v(45.88, -70.52) * mm});
            skLineSegment(sketch, "E511", {"start": v(45.88, -70.52) * mm, "end": v(47.37, -69.43) * mm});
            skLineSegment(sketch, "E512", {"start": v(47.37, -69.43) * mm, "end": v(48.74, -68.22) * mm});
            skLineSegment(sketch, "E513", {"start": v(48.74, -68.22) * mm, "end": v(49.72, -67.22) * mm});
            skLineSegment(sketch, "E514", {"start": v(49.72, -67.22) * mm, "end": v(50.92, -65.77) * mm});
            skLineSegment(sketch, "E515", {"start": v(50.92, -65.77) * mm, "end": v(52, -64.2) * mm});
            skLineSegment(sketch, "E516", {"start": v(52, -64.2) * mm, "end": v(52.92, -62.55) * mm});
            skLineSegment(sketch, "E517", {"start": v(52.92, -62.55) * mm, "end": v(53.7, -60.76) * mm});
            skLineSegment(sketch, "E518", {"start": v(53.7, -60.76) * mm, "end": v(53.73, -60.69) * mm});
            skLineSegment(sketch, "E519", {"start": v(53.73, -60.69) * mm, "end": v(54.31, -58.94) * mm});
            skLineSegment(sketch, "E520", {"start": v(54.31, -58.94) * mm, "end": v(54.77, -57.13) * mm});
            skLineSegment(sketch, "E521", {"start": v(54.77, -57.13) * mm, "end": v(55.1, -55.25) * mm});
            skLineSegment(sketch, "E522", {"start": v(55.1, -55.25) * mm, "end": v(55.3, -53.3) * mm});
            skLineSegment(sketch, "E523", {"start": v(55.3, -53.3) * mm, "end": v(55.37, -51.31) * mm});
            skLineSegment(sketch, "E524", {"start": v(55.37, -51.31) * mm, "end": v(55.37, -51.2) * mm});
            skLineSegment(sketch, "E525", {"start": v(55.37, -51.2) * mm, "end": v(55.3, -49.18) * mm});
            skLineSegment(sketch, "E526", {"start": v(55.3, -49.18) * mm, "end": v(55.09, -47.25) * mm});
            skLineSegment(sketch, "E527", {"start": v(55.09, -47.25) * mm, "end": v(54.75, -45.36) * mm});
            skLineSegment(sketch, "E528", {"start": v(54.75, -45.36) * mm, "end": v(54.26, -43.54) * mm});
            skLineSegment(sketch, "E529", {"start": v(54.26, -43.54) * mm, "end": v(53.65, -41.79) * mm});
            skLineSegment(sketch, "E530", {"start": v(53.65, -41.79) * mm, "end": v(52.9, -40.1) * mm});
            skLineSegment(sketch, "E531", {"start": v(52.9, -40.1) * mm, "end": v(52.04, -38.5) * mm});
            skLineSegment(sketch, "E532", {"start": v(52.04, -38.5) * mm, "end": v(51.87, -38.2) * mm});
            skLineSegment(sketch, "E533", {"start": v(51.87, -38.2) * mm, "end": v(50.76, -36.55) * mm});
            skLineSegment(sketch, "E534", {"start": v(50.76, -36.55) * mm, "end": v(49.57, -35.06) * mm});
            skLineSegment(sketch, "E535", {"start": v(49.57, -35.06) * mm, "end": v(48.29, -33.75) * mm});
            skLineSegment(sketch, "E536", {"start": v(48.29, -33.75) * mm, "end": v(48.14, -33.6) * mm});
            skLineSegment(sketch, "E537", {"start": v(48.14, -33.6) * mm, "end": v(46.69, -32.43) * mm});
            skLineSegment(sketch, "E538", {"start": v(46.69, -32.43) * mm, "end": v(45.07, -31.41) * mm});
            skLineSegment(sketch, "E539", {"start": v(45.07, -31.41) * mm, "end": v(43.3, -30.54) * mm});
            skLineSegment(sketch, "E540", {"start": v(27.31, -28.2) * mm, "end": v(8.33, -28.2) * mm});
            skLineSegment(sketch, "E541", {"start": v(8.33, -28.2) * mm, "end": v(8.33, -29.45) * mm});
            skLineSegment(sketch, "E542", {"start": v(8.33, -29.45) * mm, "end": v(10.09, -29.45) * mm});
            skLineSegment(sketch, "E543", {"start": v(10.09, -29.45) * mm, "end": v(10.9, -29.5) * mm});
            skLineSegment(sketch, "E544", {"start": v(10.9, -29.5) * mm, "end": v(12.74, -29.98) * mm});
            skLineSegment(sketch, "E545", {"start": v(12.74, -29.98) * mm, "end": v(14.08, -31) * mm});
            skLineSegment(sketch, "E546", {"start": v(14.08, -31) * mm, "end": v(14.6, -32.05) * mm});
            skLineSegment(sketch, "E547", {"start": v(14.6, -32.05) * mm, "end": v(14.92, -33.88) * mm});
            skLineSegment(sketch, "E548", {"start": v(14.92, -33.88) * mm, "end": v(15.04, -36.46) * mm});
            skLineSegment(sketch, "E549", {"start": v(15.04, -36.46) * mm, "end": v(15.04, -66.64) * mm});
            skLineSegment(sketch, "E550", {"start": v(15.04, -66.64) * mm, "end": v(14.98, -68.54) * mm});
            skLineSegment(sketch, "E551", {"start": v(14.98, -68.54) * mm, "end": v(14.74, -70.52) * mm});
            skLineSegment(sketch, "E552", {"start": v(14.74, -70.52) * mm, "end": v(14.28, -71.72) * mm});
            skLineSegment(sketch, "E553", {"start": v(14.28, -71.72) * mm, "end": v(13.6, -72.48) * mm});
            skLineSegment(sketch, "E554", {"start": v(13.6, -72.48) * mm, "end": v(28.97, -72.46) * mm});
            skLineSegment(sketch, "E555", {"start": v(28.97, -72.46) * mm, "end": v(27.63, -72.42) * mm});
            skLineSegment(sketch, "E556", {"start": v(27.63, -72.42) * mm, "end": v(25.85, -72.25) * mm});
            skLineSegment(sketch, "E557", {"start": v(25.85, -72.25) * mm, "end": v(23.85, -71.95) * mm});
            skLineSegment(sketch, "E558", {"start": v(23.85, -71.95) * mm, "end": v(21.65, -71.52) * mm});
            skLineSegment(sketch, "E559", {"start": v(21.65, -71.52) * mm, "end": v(21.65, -31.79) * mm});
            skLineSegment(sketch, "E560", {"start": v(21.65, -31.79) * mm, "end": v(23.15, -31.43) * mm});
            skLineSegment(sketch, "E561", {"start": v(23.15, -31.43) * mm, "end": v(25.11, -31.07) * mm});
            skLineSegment(sketch, "E562", {"start": v(25.11, -31.07) * mm, "end": v(26.97, -30.86) * mm});
            skLineSegment(sketch, "E563", {"start": v(26.97, -30.86) * mm, "end": v(28.73, -30.79) * mm});
            skLineSegment(sketch, "E564", {"start": v(28.73, -30.79) * mm, "end": v(43.3, -30.54) * mm});
            skLineSegment(sketch, "E565", {"start": v(43.3, -30.54) * mm, "end": v(42.2, -30.13) * mm});
            skLineSegment(sketch, "E566", {"start": v(42.2, -30.13) * mm, "end": v(40.46, -29.57) * mm});
            skLineSegment(sketch, "E567", {"start": v(40.46, -29.57) * mm, "end": v(38.55, -29.11) * mm});
            skLineSegment(sketch, "E568", {"start": v(38.55, -29.11) * mm, "end": v(36.5, -28.76) * mm});
            skLineSegment(sketch, "E569", {"start": v(36.5, -28.76) * mm, "end": v(35.17, -28.59) * mm});
            skLineSegment(sketch, "E570", {"start": v(35.17, -28.59) * mm, "end": v(33.4, -28.42) * mm});
            skLineSegment(sketch, "E571", {"start": v(33.4, -28.42) * mm, "end": v(31.47, -28.3) * mm});
            skLineSegment(sketch, "E572", {"start": v(31.47, -28.3) * mm, "end": v(29.46, -28.23) * mm});
            skLineSegment(sketch, "E573", {"start": v(29.46, -28.23) * mm, "end": v(27.31, -28.2) * mm});
            skLineSegment(sketch, "E574", {"start": v(17.9, 30.04) * mm, "end": v(19.3, 32.08) * mm});
            skLineSegment(sketch, "E575", {"start": v(39.6, 61.3) * mm, "end": v(39.49, 63.17) * mm});
            skLineSegment(sketch, "E576", {"start": v(39.49, 63.17) * mm, "end": v(39.05, 65.52) * mm});
            skLineSegment(sketch, "E577", {"start": v(39.05, 65.52) * mm, "end": v(38.33, 67.82) * mm});
            skLineSegment(sketch, "E578", {"start": v(38.33, 67.82) * mm, "end": v(36.54, 73.18) * mm});
            skLineSegment(sketch, "E579", {"start": v(36.54, 73.18) * mm, "end": v(38.16, 71.21) * mm});
            skLineSegment(sketch, "E580", {"start": v(38.16, 71.21) * mm, "end": v(39.4, 68.62) * mm});
            skLineSegment(sketch, "E581", {"start": v(39.4, 68.62) * mm, "end": v(39.65, 67.9) * mm});
            skLineSegment(sketch, "E582", {"start": v(39.65, 67.9) * mm, "end": v(40.27, 65.65) * mm});
            skLineSegment(sketch, "E583", {"start": v(40.27, 65.65) * mm, "end": v(40.62, 63.3) * mm});
            skLineSegment(sketch, "E584", {"start": v(40.62, 63.3) * mm, "end": v(40.69, 61.63) * mm});
            skLineSegment(sketch, "E585", {"start": v(46.53, 63.67) * mm, "end": v(45.76, 63.65) * mm});
            skLineSegment(sketch, "E586", {"start": v(45.76, 63.65) * mm, "end": v(43.45, 63.44) * mm});
            skLineSegment(sketch, "E587", {"start": v(43.45, 63.44) * mm, "end": v(41.13, 62.95) * mm});
            skLineSegment(sketch, "E588", {"start": v(41.4, 61.84) * mm, "end": v(43.75, 62.26) * mm});
            skLineSegment(sketch, "E589", {"start": v(43.75, 62.26) * mm, "end": v(46.16, 62.39) * mm});
            skLineSegment(sketch, "E590", {"start": v(46.16, 62.39) * mm, "end": v(51.8, 62.58) * mm});
            skLineSegment(sketch, "E591", {"start": v(51.8, 62.58) * mm, "end": v(49.4, 63.4) * mm});
            skLineSegment(sketch, "E592", {"start": v(49.4, 63.4) * mm, "end": v(46.53, 63.67) * mm});
            skLineSegment(sketch, "E593", {"start": v(41.13, 62.95) * mm, "end": v(40.64, 62.83) * mm});
            skLineSegment(sketch, "E594", {"start": v(41.4, 61.84) * mm, "end": v(39.6, 61.3) * mm});
            skLineSegment(sketch, "E595", {"start": v(17.9, 30.04) * mm, "end": v(17.62, 31.85) * mm});
            skLineSegment(sketch, "E596", {"start": v(17.62, 31.85) * mm, "end": v(17.27, 35.33) * mm});
            skLineSegment(sketch, "E597", {"start": v(17.27, 35.33) * mm, "end": v(16.99, 38.79) * mm});
            skLineSegment(sketch, "E598", {"start": v(16.99, 38.79) * mm, "end": v(16.79, 42.07) * mm});
            skLineSegment(sketch, "E599", {"start": v(16.79, 42.07) * mm, "end": v(16.66, 45.16) * mm});
            skLineSegment(sketch, "E600", {"start": v(16.66, 45.16) * mm, "end": v(16.63, 48.06) * mm});
            skLineSegment(sketch, "E601", {"start": v(16.63, 48.06) * mm, "end": v(16.67, 50.79) * mm});
            skLineSegment(sketch, "E602", {"start": v(16.67, 50.79) * mm, "end": v(16.81, 53.33) * mm});
            skLineSegment(sketch, "E603", {"start": v(16.81, 53.33) * mm, "end": v(17.04, 55.68) * mm});
            skLineSegment(sketch, "E604", {"start": v(17.04, 55.68) * mm, "end": v(17.34, 57.85) * mm});
            skLineSegment(sketch, "E605", {"start": v(17.34, 57.85) * mm, "end": v(17.72, 59.84) * mm});
            skLineSegment(sketch, "E606", {"start": v(17.72, 59.84) * mm, "end": v(18.2, 61.64) * mm});
            skLineSegment(sketch, "E607", {"start": v(18.2, 61.64) * mm, "end": v(18.74, 63.25) * mm});
            skLineSegment(sketch, "E608", {"start": v(18.74, 63.25) * mm, "end": v(20.03, 66.04) * mm});
            skLineSegment(sketch, "E609", {"start": v(20.03, 66.04) * mm, "end": v(21.44, 68.5) * mm});
            skLineSegment(sketch, "E610", {"start": v(21.44, 68.5) * mm, "end": v(23.04, 70.58) * mm});
            skLineSegment(sketch, "E611", {"start": v(23.04, 70.58) * mm, "end": v(24.77, 72.3) * mm});
            skLineSegment(sketch, "E612", {"start": v(24.77, 72.3) * mm, "end": v(26.66, 73.64) * mm});
            skLineSegment(sketch, "E613", {"start": v(26.66, 73.64) * mm, "end": v(28.71, 74.6) * mm});
            skLineSegment(sketch, "E614", {"start": v(28.71, 74.6) * mm, "end": v(30.02, 74.99) * mm});
            skLineSegment(sketch, "E615", {"start": v(30.02, 74.99) * mm, "end": v(32.56, 75.11) * mm});
            skLineSegment(sketch, "E616", {"start": v(32.56, 75.11) * mm, "end": v(34.96, 74.34) * mm});
            skLineSegment(sketch, "E617", {"start": v(34.96, 74.34) * mm, "end": v(36.54, 73.18) * mm});
            skLineSegment(sketch, "E618", {"start": v(36.54, 73.18) * mm, "end": v(38.33, 67.82) * mm});
            skLineSegment(sketch, "E619", {"start": v(38.33, 67.82) * mm, "end": v(37.1, 70.45) * mm});
            skLineSegment(sketch, "E620", {"start": v(37.1, 70.45) * mm, "end": v(35.56, 72.35) * mm});
            skLineSegment(sketch, "E621", {"start": v(35.56, 72.35) * mm, "end": v(33.75, 73.43) * mm});
            skLineSegment(sketch, "E622", {"start": v(33.75, 73.43) * mm, "end": v(31.7, 73.73) * mm});
            skLineSegment(sketch, "E623", {"start": v(31.7, 73.73) * mm, "end": v(29.37, 73.22) * mm});
            skLineSegment(sketch, "E624", {"start": v(29.37, 73.22) * mm, "end": v(27.98, 72.58) * mm});
            skLineSegment(sketch, "E625", {"start": v(27.98, 72.58) * mm, "end": v(26.13, 71.4) * mm});
            skLineSegment(sketch, "E626", {"start": v(26.13, 71.4) * mm, "end": v(24.47, 69.8) * mm});
            skLineSegment(sketch, "E627", {"start": v(24.47, 69.8) * mm, "end": v(22.96, 67.88) * mm});
            skLineSegment(sketch, "E628", {"start": v(22.96, 67.88) * mm, "end": v(21.64, 65.56) * mm});
            skLineSegment(sketch, "E629", {"start": v(21.64, 65.56) * mm, "end": v(20.48, 62.9) * mm});
            skLineSegment(sketch, "E630", {"start": v(20.48, 62.9) * mm, "end": v(19.47, 59.84) * mm});
            skLineSegment(sketch, "E631", {"start": v(19.47, 59.84) * mm, "end": v(19.18, 58.67) * mm});
            skLineSegment(sketch, "E632", {"start": v(19.18, 58.67) * mm, "end": v(18.7, 56.49) * mm});
            skLineSegment(sketch, "E633", {"start": v(18.7, 56.49) * mm, "end": v(18.35, 54.2) * mm});
            skLineSegment(sketch, "E634", {"start": v(18.35, 54.2) * mm, "end": v(18.1, 51.8) * mm});
            skLineSegment(sketch, "E635", {"start": v(18.1, 51.8) * mm, "end": v(17.97, 49.3) * mm});
            skLineSegment(sketch, "E636", {"start": v(17.97, 49.3) * mm, "end": v(17.92, 46.69) * mm});
            skLineSegment(sketch, "E637", {"start": v(17.92, 46.69) * mm, "end": v(17.99, 43.98) * mm});
            skLineSegment(sketch, "E638", {"start": v(17.99, 43.98) * mm, "end": v(18.17, 41.16) * mm});
            skLineSegment(sketch, "E639", {"start": v(18.17, 41.16) * mm, "end": v(18.44, 38.24) * mm});
            skLineSegment(sketch, "E640", {"start": v(18.44, 38.24) * mm, "end": v(18.82, 35.21) * mm});
            skLineSegment(sketch, "E641", {"start": v(18.82, 35.21) * mm, "end": v(19.3, 32.08) * mm});
            skLineSegment(sketch, "E642", {"start": v(19.3, 32.08) * mm, "end": v(19.33, 30.57) * mm});
            skLineSegment(sketch, "E643", {"start": v(19.33, 30.57) * mm, "end": v(19.35, 30.35) * mm});
            skSolve(sketch);
        }
        {
            var Q0;
            {var subQ1=sQuery(id+"F0.wireOp",EDGE,"E323");Q0=makeQuery(id+"F0.imprint","IMPRINT",FACE,{"disambiguationData":[TD([[makeQuery(id+"F0.imprint","IMPRINT",EDGE,{"derivedFrom":subQ1}),-1.0]])]});}
            var Q1;
            Q1=makeQuery(id+"F0.imprint","IMPRINT",FACE,{"disambiguationData":[TD([[makeQuery(id+"F0.imprint","IMPRINT",EDGE,{"derivedFrom":sQuery(id+"F0.wireOp",EDGE,"E406")}),1.0]])]});
            var Q2;
            {var subQ0=sQuery(id+"F0.wireOp",EDGE,"E328");Q2=makeQuery(id+"F0.imprint","IMPRINT",FACE,{"disambiguationData":[TD([[makeQuery(id+"F0.imprint","IMPRINT",EDGE,{"derivedFrom":subQ0}),1.0]])]});}
            var Q3;
            {var subQ4=sQuery(id+"F0.wireOp",EDGE,"E323");Q3=makeQuery(id+"F0.imprint","IMPRINT",FACE,{"disambiguationData":[TD([[makeQuery(id+"F0.imprint","IMPRINT",EDGE,{"derivedFrom":subQ4}),1.0]])]});}
            var Q4;
            {var subQ4=sQuery(id+"F0.wireOp",EDGE,"E321");Q4=makeQuery(id+"F0.imprint","IMPRINT",FACE,{"disambiguationData":[TD([[makeQuery(id+"F0.imprint","IMPRINT",EDGE,{"derivedFrom":subQ4}),1.0]])]});}
            var Q5;
            Q5=makeQuery(id+"F0.imprint","IMPRINT",FACE,{"disambiguationData":[TD([[makeQuery(id+"F0.imprint","IMPRINT",EDGE,{"derivedFrom":sQuery(id+"F0.wireOp",EDGE,"E296")}),1.0]])]});
            var Q6;
            {var subQ0=sQuery(id+"F0.wireOp",EDGE,"E574");Q6=makeQuery(id+"F0.imprint","IMPRINT",FACE,{"disambiguationData":[TD([[makeQuery(id+"F0.imprint","IMPRINT",EDGE,{"derivedFrom":subQ0}),-1.0]])]});}
            var Q7;
            {var subQ0=sQuery(id+"F0.wireOp",EDGE,"E319");Q7=makeQuery(id+"F0.imprint","IMPRINT",FACE,{"disambiguationData":[TD([[makeQuery(id+"F0.imprint","IMPRINT",EDGE,{"derivedFrom":subQ0}),1.0]])]});}
            var Q8;
            {var subQ4=sQuery(id+"F0.wireOp",EDGE,"E319");Q8=makeQuery(id+"F0.imprint","IMPRINT",FACE,{"disambiguationData":[TD([[makeQuery(id+"F0.imprint","IMPRINT",EDGE,{"derivedFrom":subQ4}),-1.0]])]});}
            var Q9;
            Q9=makeQuery(id+"F0.imprint","IMPRINT",FACE,{"disambiguationData":[TD([[makeQuery(id+"F0.imprint","IMPRINT",EDGE,{"derivedFrom":sQuery(id+"F0.wireOp",EDGE,"E585")}),1.0]])]});
            var Q10;
            {var subQ3=sQuery(id+"F0.wireOp",EDGE,"E575");Q10=makeQuery(id+"F0.imprint","IMPRINT",FACE,{"disambiguationData":[TD([[makeQuery(id+"F0.imprint","IMPRINT",EDGE,{"derivedFrom":subQ3}),-1.0]])]});}
            var Q11;
            {var subQ6=sQuery(id+"F0.wireOp",EDGE,"E104");Q11=makeQuery(id+"F0.imprint","IMPRINT",FACE,{"disambiguationData":[TD([[makeQuery(id+"F0.imprint","IMPRINT",EDGE,{"derivedFrom":subQ6}),1.0]])]});}
            var Q12;
            Q12=makeQuery(id+"F0.imprint","IMPRINT",FACE,{"disambiguationData":[TD([[makeQuery(id+"F0.imprint","IMPRINT",EDGE,{"derivedFrom":sQuery(id+"F0.wireOp",EDGE,"E71")}),1.0]])]});
            var Q13;
            Q13=makeQuery(id+"F0.imprint","IMPRINT",FACE,{"disambiguationData":[TD([[makeQuery(id+"F0.imprint","IMPRINT",EDGE,{"derivedFrom":sQuery(id+"F0.wireOp",EDGE,"E253")}),1.0]])]});
            var Q14;
            Q14=makeQuery(id+"F0.imprint","IMPRINT",FACE,{"disambiguationData":[TD([[makeQuery(id+"F0.imprint","IMPRINT",EDGE,{"derivedFrom":sQuery(id+"F0.wireOp",EDGE,"E224")}),1.0]])]});
            var Q15;
            {var subQ5=sQuery(id+"F0.wireOp",EDGE,"E192");Q15=makeQuery(id+"F0.imprint","IMPRINT",FACE,{"disambiguationData":[TD([[makeQuery(id+"F0.imprint","IMPRINT",EDGE,{"derivedFrom":subQ5}),1.0]])]});}
            var Q16;
            {var subQ0=sQuery(id+"F0.wireOp",EDGE,"E541");Q16=makeQuery(id+"F0.imprint","IMPRINT",FACE,{"disambiguationData":[TD([[makeQuery(id+"F0.imprint","IMPRINT",EDGE,{"derivedFrom":subQ0}),1.0]])]});}
            var Q17;
            {var subQ0=sQuery(id+"F0.wireOp",EDGE,"E128");Q17=makeQuery(id+"F0.imprint","IMPRINT",FACE,{"disambiguationData":[TD([[makeQuery(id+"F0.imprint","IMPRINT",EDGE,{"derivedFrom":subQ0}),1.0]])]});}
            var Q18;
            {var subQ7=sQuery(id+"F0.wireOp",EDGE,"E561");Q18=makeQuery(id+"F0.imprint","IMPRINT",FACE,{"disambiguationData":[TD([[makeQuery(id+"F0.imprint","IMPRINT",EDGE,{"derivedFrom":subQ7}),1.0]])]});}
            var Q19;
            Q19=makeQuery(id+"F0.imprint","IMPRINT",FACE,{"disambiguationData":[TD([[makeQuery(id+"F0.imprint","IMPRINT",EDGE,{"derivedFrom":sQuery(id+"F0.wireOp",EDGE,"E457")}),1.0]])]});
            var Q20;
            {var subQ9=sQuery(id+"F0.wireOp",EDGE,"E192");Q20=makeQuery(id+"F0.imprint","IMPRINT",FACE,{"disambiguationData":[TD([[makeQuery(id+"F0.imprint","IMPRINT",EDGE,{"derivedFrom":subQ9}),-1.0]])]});}
            var Q21;
            Q21=makeQuery(id+"F0.imprint","IMPRINT",FACE,{"disambiguationData":[TD([[makeQuery(id+"F0.imprint","IMPRINT",EDGE,{"derivedFrom":sQuery(id+"F0.wireOp",EDGE,"E0")}),1.0]])]});
            var Q22;
            Q22=makeQuery(id+"F0.imprint","IMPRINT",FACE,{"disambiguationData":[TD([[makeQuery(id+"F0.imprint","IMPRINT",EDGE,{"derivedFrom":sQuery(id+"F0.wireOp",EDGE,"E53")}),1.0]])]});
            var Q23;
            {var subQ5=sQuery(id+"F0.wireOp",EDGE,"E372");Q23=makeQuery(id+"F0.imprint","IMPRINT",FACE,{"disambiguationData":[TD([[makeQuery(id+"F0.imprint","IMPRINT",EDGE,{"derivedFrom":subQ5}),-1.0]])]});}
            extrude(context, id + "F1", {"entities" : qUnion([Q0, Q1, Q2, Q3, Q4, Q5, Q6, Q7, Q8, Q9, Q10, Q11, Q12, Q13, Q14, Q15, Q16, Q17, Q18, Q19, Q20, Q21, Q22, Q23]), "depth" : 10 * mm});
        }
        {
            var Q0;
            Q0=makeQuery(id+"F1.opExtrude","CAP_FACE",FACE,{"disambiguationData":[OSD([sQuery(id+"F0.wireOp",EDGE,"E0"),sQuery(id+"F0.wireOp",EDGE,"E1"),sQuery(id+"F0.wireOp",EDGE,"E2"),sQuery(id+"F0.wireOp",EDGE,"E3"),sQuery(id+"F0.wireOp",EDGE,"E4"),sQuery(id+"F0.wireOp",EDGE,"E5"),sQuery(id+"F0.wireOp",EDGE,"E6"),sQuery(id+"F0.wireOp",EDGE,"E7"),sQuery(id+"F0.wireOp",EDGE,"E8"),sQuery(id+"F0.wireOp",EDGE,"E9"),sQuery(id+"F0.wireOp",EDGE,"E10"),sQuery(id+"F0.wireOp",EDGE,"E11"),sQuery(id+"F0.wireOp",EDGE,"E12"),sQuery(id+"F0.wireOp",EDGE,"E13"),sQuery(id+"F0.wireOp",EDGE,"E14"),sQuery(id+"F0.wireOp",EDGE,"E15"),sQuery(id+"F0.wireOp",EDGE,"E16"),sQuery(id+"F0.wireOp",EDGE,"E17"),sQuery(id+"F0.wireOp",EDGE,"E18"),sQuery(id+"F0.wireOp",EDGE,"E19"),sQuery(id+"F0.wireOp",EDGE,"E20"),sQuery(id+"F0.wireOp",EDGE,"E21"),sQuery(id+"F0.wireOp",EDGE,"E23"),sQuery(id+"F0.wireOp",EDGE,"E24"),sQuery(id+"F0.wireOp",EDGE,"E25"),sQuery(id+"F0.wireOp",EDGE,"E26"),sQuery(id+"F0.wireOp",EDGE,"E27"),sQuery(id+"F0.wireOp",EDGE,"E28"),sQuery(id+"F0.wireOp",EDGE,"E29"),sQuery(id+"F0.wireOp",EDGE,"E30"),sQuery(id+"F0.wireOp",EDGE,"E31"),sQuery(id+"F0.wireOp",EDGE,"E32"),sQuery(id+"F0.wireOp",EDGE,"E33"),sQuery(id+"F0.wireOp",EDGE,"E34"),sQuery(id+"F0.wireOp",EDGE,"E35"),sQuery(id+"F0.wireOp",EDGE,"E36"),sQuery(id+"F0.wireOp",EDGE,"E37"),sQuery(id+"F0.wireOp",EDGE,"E38"),sQuery(id+"F0.wireOp",EDGE,"E39"),sQuery(id+"F0.wireOp",EDGE,"E40"),sQuery(id+"F0.wireOp",EDGE,"E41"),sQuery(id+"F0.wireOp",EDGE,"E42"),sQuery(id+"F0.wireOp",EDGE,"E43"),sQuery(id+"F0.wireOp",EDGE,"E44"),sQuery(id+"F0.wireOp",EDGE,"E45"),sQuery(id+"F0.wireOp",EDGE,"E46"),sQuery(id+"F0.wireOp",EDGE,"E47"),sQuery(id+"F0.wireOp",EDGE,"E48"),sQuery(id+"F0.wireOp",EDGE,"E49"),sQuery(id+"F0.wireOp",EDGE,"E50"),sQuery(id+"F0.wireOp",EDGE,"E51"),sQuery(id+"F0.wireOp",EDGE,"E53"),sQuery(id+"F0.wireOp",EDGE,"E54"),sQuery(id+"F0.wireOp",EDGE,"E55"),sQuery(id+"F0.wireOp",EDGE,"E56"),sQuery(id+"F0.wireOp",EDGE,"E58"),sQuery(id+"F0.wireOp",EDGE,"E59"),sQuery(id+"F0.wireOp",EDGE,"E60"),sQuery(id+"F0.wireOp",EDGE,"E61"),sQuery(id+"F0.wireOp",EDGE,"E62"),sQuery(id+"F0.wireOp",EDGE,"E63"),sQuery(id+"F0.wireOp",EDGE,"E64"),sQuery(id+"F0.wireOp",EDGE,"E65"),sQuery(id+"F0.wireOp",EDGE,"E66"),sQuery(id+"F0.wireOp",EDGE,"E67"),sQuery(id+"F0.wireOp",EDGE,"E68"),sQuery(id+"F0.wireOp",EDGE,"E69"),sQuery(id+"F0.wireOp",EDGE,"E70"),sQuery(id+"F0.wireOp",EDGE,"E71"),sQuery(id+"F0.wireOp",EDGE,"E72"),sQuery(id+"F0.wireOp",EDGE,"E73"),sQuery(id+"F0.wireOp",EDGE,"E74"),sQuery(id+"F0.wireOp",EDGE,"E75"),sQuery(id+"F0.wireOp",EDGE,"E76"),sQuery(id+"F0.wireOp",EDGE,"E77"),sQuery(id+"F0.wireOp",EDGE,"E78"),sQuery(id+"F0.wireOp",EDGE,"E79"),sQuery(id+"F0.wireOp",EDGE,"E80"),sQuery(id+"F0.wireOp",EDGE,"E81"),sQuery(id+"F0.wireOp",EDGE,"E82"),sQuery(id+"F0.wireOp",EDGE,"E83"),sQuery(id+"F0.wireOp",EDGE,"E84"),sQuery(id+"F0.wireOp",EDGE,"E85"),sQuery(id+"F0.wireOp",EDGE,"E86"),sQuery(id+"F0.wireOp",EDGE,"E88"),sQuery(id+"F0.wireOp",EDGE,"E89"),sQuery(id+"F0.wireOp",EDGE,"E90"),sQuery(id+"F0.wireOp",EDGE,"E91"),sQuery(id+"F0.wireOp",EDGE,"E92"),sQuery(id+"F0.wireOp",EDGE,"E93"),sQuery(id+"F0.wireOp",EDGE,"E94"),sQuery(id+"F0.wireOp",EDGE,"E95"),sQuery(id+"F0.wireOp",EDGE,"E96"),sQuery(id+"F0.wireOp",EDGE,"E97"),sQuery(id+"F0.wireOp",EDGE,"E98"),sQuery(id+"F0.wireOp",EDGE,"E99"),sQuery(id+"F0.wireOp",EDGE,"E100"),sQuery(id+"F0.wireOp",EDGE,"E101"),sQuery(id+"F0.wireOp",EDGE,"E104"),sQuery(id+"F0.wireOp",EDGE,"E105"),sQuery(id+"F0.wireOp",EDGE,"E106"),sQuery(id+"F0.wireOp",EDGE,"E107"),sQuery(id+"F0.wireOp",EDGE,"E108"),sQuery(id+"F0.wireOp",EDGE,"E109"),sQuery(id+"F0.wireOp",EDGE,"E110"),sQuery(id+"F0.wireOp",EDGE,"E112"),sQuery(id+"F0.wireOp",EDGE,"E113"),sQuery(id+"F0.wireOp",EDGE,"E114"),sQuery(id+"F0.wireOp",EDGE,"E115"),sQuery(id+"F0.wireOp",EDGE,"E116"),sQuery(id+"F0.wireOp",EDGE,"E117"),sQuery(id+"F0.wireOp",EDGE,"E118"),sQuery(id+"F0.wireOp",EDGE,"E119"),sQuery(id+"F0.wireOp",EDGE,"E120"),sQuery(id+"F0.wireOp",EDGE,"E121"),sQuery(id+"F0.wireOp",EDGE,"E122"),sQuery(id+"F0.wireOp",EDGE,"E123"),sQuery(id+"F0.wireOp",EDGE,"E124"),sQuery(id+"F0.wireOp",EDGE,"E125"),sQuery(id+"F0.wireOp",EDGE,"E126"),sQuery(id+"F0.wireOp",EDGE,"E127"),sQuery(id+"F0.wireOp",EDGE,"E128"),sQuery(id+"F0.wireOp",EDGE,"E129"),sQuery(id+"F0.wireOp",EDGE,"E130"),sQuery(id+"F0.wireOp",EDGE,"E131"),sQuery(id+"F0.wireOp",EDGE,"E132"),sQuery(id+"F0.wireOp",EDGE,"E133"),sQuery(id+"F0.wireOp",EDGE,"E134"),sQuery(id+"F0.wireOp",EDGE,"E135"),sQuery(id+"F0.wireOp",EDGE,"E136"),sQuery(id+"F0.wireOp",EDGE,"E137"),sQuery(id+"F0.wireOp",EDGE,"E138"),sQuery(id+"F0.wireOp",EDGE,"E139"),sQuery(id+"F0.wireOp",EDGE,"E140"),sQuery(id+"F0.wireOp",EDGE,"E141"),sQuery(id+"F0.wireOp",EDGE,"E142"),sQuery(id+"F0.wireOp",EDGE,"E143"),sQuery(id+"F0.wireOp",EDGE,"E144"),sQuery(id+"F0.wireOp",EDGE,"E145"),sQuery(id+"F0.wireOp",EDGE,"E146"),sQuery(id+"F0.wireOp",EDGE,"E147"),sQuery(id+"F0.wireOp",EDGE,"E148"),sQuery(id+"F0.wireOp",EDGE,"E149"),sQuery(id+"F0.wireOp",EDGE,"E150"),sQuery(id+"F0.wireOp",EDGE,"E151"),sQuery(id+"F0.wireOp",EDGE,"E152"),sQuery(id+"F0.wireOp",EDGE,"E153"),sQuery(id+"F0.wireOp",EDGE,"E154"),sQuery(id+"F0.wireOp",EDGE,"E155"),sQuery(id+"F0.wireOp",EDGE,"E156"),sQuery(id+"F0.wireOp",EDGE,"E158"),sQuery(id+"F0.wireOp",EDGE,"E159"),sQuery(id+"F0.wireOp",EDGE,"E160"),sQuery(id+"F0.wireOp",EDGE,"E161"),sQuery(id+"F0.wireOp",EDGE,"E162"),sQuery(id+"F0.wireOp",EDGE,"E163"),sQuery(id+"F0.wireOp",EDGE,"E164"),sQuery(id+"F0.wireOp",EDGE,"E165"),sQuery(id+"F0.wireOp",EDGE,"E166"),sQuery(id+"F0.wireOp",EDGE,"E167"),sQuery(id+"F0.wireOp",EDGE,"E168"),sQuery(id+"F0.wireOp",EDGE,"E169"),sQuery(id+"F0.wireOp",EDGE,"E170"),sQuery(id+"F0.wireOp",EDGE,"E171"),sQuery(id+"F0.wireOp",EDGE,"E172"),sQuery(id+"F0.wireOp",EDGE,"E173"),sQuery(id+"F0.wireOp",EDGE,"E174"),sQuery(id+"F0.wireOp",EDGE,"E175"),sQuery(id+"F0.wireOp",EDGE,"E176"),sQuery(id+"F0.wireOp",EDGE,"E177"),sQuery(id+"F0.wireOp",EDGE,"E178"),sQuery(id+"F0.wireOp",EDGE,"E179"),sQuery(id+"F0.wireOp",EDGE,"E180"),sQuery(id+"F0.wireOp",EDGE,"E181"),sQuery(id+"F0.wireOp",EDGE,"E182"),sQuery(id+"F0.wireOp",EDGE,"E183"),sQuery(id+"F0.wireOp",EDGE,"E184"),sQuery(id+"F0.wireOp",EDGE,"E185"),sQuery(id+"F0.wireOp",EDGE,"E186"),sQuery(id+"F0.wireOp",EDGE,"E187"),sQuery(id+"F0.wireOp",EDGE,"E188"),sQuery(id+"F0.wireOp",EDGE,"E189"),sQuery(id+"F0.wireOp",EDGE,"E190"),sQuery(id+"F0.wireOp",EDGE,"E191"),sQuery(id+"F0.wireOp",EDGE,"E198"),sQuery(id+"F0.wireOp",EDGE,"E199"),sQuery(id+"F0.wireOp",EDGE,"E200"),sQuery(id+"F0.wireOp",EDGE,"E201"),sQuery(id+"F0.wireOp",EDGE,"E202"),sQuery(id+"F0.wireOp",EDGE,"E203"),sQuery(id+"F0.wireOp",EDGE,"E204"),sQuery(id+"F0.wireOp",EDGE,"E205"),sQuery(id+"F0.wireOp",EDGE,"E206"),sQuery(id+"F0.wireOp",EDGE,"E207"),sQuery(id+"F0.wireOp",EDGE,"E208"),sQuery(id+"F0.wireOp",EDGE,"E209"),sQuery(id+"F0.wireOp",EDGE,"E210"),sQuery(id+"F0.wireOp",EDGE,"E211"),sQuery(id+"F0.wireOp",EDGE,"E212"),sQuery(id+"F0.wireOp",EDGE,"E213"),sQuery(id+"F0.wireOp",EDGE,"E215"),sQuery(id+"F0.wireOp",EDGE,"E216"),sQuery(id+"F0.wireOp",EDGE,"E217"),sQuery(id+"F0.wireOp",EDGE,"E218"),sQuery(id+"F0.wireOp",EDGE,"E219"),sQuery(id+"F0.wireOp",EDGE,"E220"),sQuery(id+"F0.wireOp",EDGE,"E221"),sQuery(id+"F0.wireOp",EDGE,"E222"),sQuery(id+"F0.wireOp",EDGE,"E224"),sQuery(id+"F0.wireOp",EDGE,"E225"),sQuery(id+"F0.wireOp",EDGE,"E226"),sQuery(id+"F0.wireOp",EDGE,"E227"),sQuery(id+"F0.wireOp",EDGE,"E228"),sQuery(id+"F0.wireOp",EDGE,"E229"),sQuery(id+"F0.wireOp",EDGE,"E230"),sQuery(id+"F0.wireOp",EDGE,"E231"),sQuery(id+"F0.wireOp",EDGE,"E232"),sQuery(id+"F0.wireOp",EDGE,"E233"),sQuery(id+"F0.wireOp",EDGE,"E234"),sQuery(id+"F0.wireOp",EDGE,"E235"),sQuery(id+"F0.wireOp",EDGE,"E236"),sQuery(id+"F0.wireOp",EDGE,"E237"),sQuery(id+"F0.wireOp",EDGE,"E238"),sQuery(id+"F0.wireOp",EDGE,"E239"),sQuery(id+"F0.wireOp",EDGE,"E240"),sQuery(id+"F0.wireOp",EDGE,"E241"),sQuery(id+"F0.wireOp",EDGE,"E242"),sQuery(id+"F0.wireOp",EDGE,"E243"),sQuery(id+"F0.wireOp",EDGE,"E244"),sQuery(id+"F0.wireOp",EDGE,"E245"),sQuery(id+"F0.wireOp",EDGE,"E246"),sQuery(id+"F0.wireOp",EDGE,"E247"),sQuery(id+"F0.wireOp",EDGE,"E248"),sQuery(id+"F0.wireOp",EDGE,"E249"),sQuery(id+"F0.wireOp",EDGE,"E250"),sQuery(id+"F0.wireOp",EDGE,"E251"),sQuery(id+"F0.wireOp",EDGE,"E252"),sQuery(id+"F0.wireOp",EDGE,"E253"),sQuery(id+"F0.wireOp",EDGE,"E254"),sQuery(id+"F0.wireOp",EDGE,"E255"),sQuery(id+"F0.wireOp",EDGE,"E256"),sQuery(id+"F0.wireOp",EDGE,"E257"),sQuery(id+"F0.wireOp",EDGE,"E258"),sQuery(id+"F0.wireOp",EDGE,"E259"),sQuery(id+"F0.wireOp",EDGE,"E260"),sQuery(id+"F0.wireOp",EDGE,"E261"),sQuery(id+"F0.wireOp",EDGE,"E262"),sQuery(id+"F0.wireOp",EDGE,"E263"),sQuery(id+"F0.wireOp",EDGE,"E264"),sQuery(id+"F0.wireOp",EDGE,"E265"),sQuery(id+"F0.wireOp",EDGE,"E266"),sQuery(id+"F0.wireOp",EDGE,"E267"),sQuery(id+"F0.wireOp",EDGE,"E268"),sQuery(id+"F0.wireOp",EDGE,"E269"),sQuery(id+"F0.wireOp",EDGE,"E270"),sQuery(id+"F0.wireOp",EDGE,"E271"),sQuery(id+"F0.wireOp",EDGE,"E273"),sQuery(id+"F0.wireOp",EDGE,"E274"),sQuery(id+"F0.wireOp",EDGE,"E275"),sQuery(id+"F0.wireOp",EDGE,"E276"),sQuery(id+"F0.wireOp",EDGE,"E277"),sQuery(id+"F0.wireOp",EDGE,"E278"),sQuery(id+"F0.wireOp",EDGE,"E279"),sQuery(id+"F0.wireOp",EDGE,"E280"),sQuery(id+"F0.wireOp",EDGE,"E281"),sQuery(id+"F0.wireOp",EDGE,"E282"),sQuery(id+"F0.wireOp",EDGE,"E283"),sQuery(id+"F0.wireOp",EDGE,"E284"),sQuery(id+"F0.wireOp",EDGE,"E285"),sQuery(id+"F0.wireOp",EDGE,"E286"),sQuery(id+"F0.wireOp",EDGE,"E287"),sQuery(id+"F0.wireOp",EDGE,"E288"),sQuery(id+"F0.wireOp",EDGE,"E289"),sQuery(id+"F0.wireOp",EDGE,"E290"),sQuery(id+"F0.wireOp",EDGE,"E291"),sQuery(id+"F0.wireOp",EDGE,"E293"),sQuery(id+"F0.wireOp",EDGE,"E294"),sQuery(id+"F0.wireOp",EDGE,"E296"),sQuery(id+"F0.wireOp",EDGE,"E297"),sQuery(id+"F0.wireOp",EDGE,"E298"),sQuery(id+"F0.wireOp",EDGE,"E299"),sQuery(id+"F0.wireOp",EDGE,"E300"),sQuery(id+"F0.wireOp",EDGE,"E301"),sQuery(id+"F0.wireOp",EDGE,"E302"),sQuery(id+"F0.wireOp",EDGE,"E303"),sQuery(id+"F0.wireOp",EDGE,"E304"),sQuery(id+"F0.wireOp",EDGE,"E305"),sQuery(id+"F0.wireOp",EDGE,"E306"),sQuery(id+"F0.wireOp",EDGE,"E307"),sQuery(id+"F0.wireOp",EDGE,"E308"),sQuery(id+"F0.wireOp",EDGE,"E309"),sQuery(id+"F0.wireOp",EDGE,"E310"),sQuery(id+"F0.wireOp",EDGE,"E311"),sQuery(id+"F0.wireOp",EDGE,"E312"),sQuery(id+"F0.wireOp",EDGE,"E313"),sQuery(id+"F0.wireOp",EDGE,"E314"),sQuery(id+"F0.wireOp",EDGE,"E315"),sQuery(id+"F0.wireOp",EDGE,"E316"),sQuery(id+"F0.wireOp",EDGE,"E317"),sQuery(id+"F0.wireOp",EDGE,"E318"),sQuery(id+"F0.wireOp",EDGE,"E320"),sQuery(id+"F0.wireOp",EDGE,"E321"),sQuery(id+"F0.wireOp",EDGE,"E322"),sQuery(id+"F0.wireOp",EDGE,"E327"),sQuery(id+"F0.wireOp",EDGE,"E328"),sQuery(id+"F0.wireOp",EDGE,"E329"),sQuery(id+"F0.wireOp",EDGE,"E330"),sQuery(id+"F0.wireOp",EDGE,"E331"),sQuery(id+"F0.wireOp",EDGE,"E332"),sQuery(id+"F0.wireOp",EDGE,"E333"),sQuery(id+"F0.wireOp",EDGE,"E334"),sQuery(id+"F0.wireOp",EDGE,"E335"),sQuery(id+"F0.wireOp",EDGE,"E336"),sQuery(id+"F0.wireOp",EDGE,"E337"),sQuery(id+"F0.wireOp",EDGE,"E338"),sQuery(id+"F0.wireOp",EDGE,"E339"),sQuery(id+"F0.wireOp",EDGE,"E340"),sQuery(id+"F0.wireOp",EDGE,"E341"),sQuery(id+"F0.wireOp",EDGE,"E342"),sQuery(id+"F0.wireOp",EDGE,"E343"),sQuery(id+"F0.wireOp",EDGE,"E344"),sQuery(id+"F0.wireOp",EDGE,"E345"),sQuery(id+"F0.wireOp",EDGE,"E346"),sQuery(id+"F0.wireOp",EDGE,"E347"),sQuery(id+"F0.wireOp",EDGE,"E348"),sQuery(id+"F0.wireOp",EDGE,"E349"),sQuery(id+"F0.wireOp",EDGE,"E350"),sQuery(id+"F0.wireOp",EDGE,"E351"),sQuery(id+"F0.wireOp",EDGE,"E353"),sQuery(id+"F0.wireOp",EDGE,"E354"),sQuery(id+"F0.wireOp",EDGE,"E355"),sQuery(id+"F0.wireOp",EDGE,"E356"),sQuery(id+"F0.wireOp",EDGE,"E357"),sQuery(id+"F0.wireOp",EDGE,"E358"),sQuery(id+"F0.wireOp",EDGE,"E359"),sQuery(id+"F0.wireOp",EDGE,"E360"),sQuery(id+"F0.wireOp",EDGE,"E361"),sQuery(id+"F0.wireOp",EDGE,"E362"),sQuery(id+"F0.wireOp",EDGE,"E363"),sQuery(id+"F0.wireOp",EDGE,"E364"),sQuery(id+"F0.wireOp",EDGE,"E365"),sQuery(id+"F0.wireOp",EDGE,"E366"),sQuery(id+"F0.wireOp",EDGE,"E367"),sQuery(id+"F0.wireOp",EDGE,"E368"),sQuery(id+"F0.wireOp",EDGE,"E369"),sQuery(id+"F0.wireOp",EDGE,"E370"),sQuery(id+"F0.wireOp",EDGE,"E371"),sQuery(id+"F0.wireOp",EDGE,"E373"),sQuery(id+"F0.wireOp",EDGE,"E374"),sQuery(id+"F0.wireOp",EDGE,"E375"),sQuery(id+"F0.wireOp",EDGE,"E376"),sQuery(id+"F0.wireOp",EDGE,"E377"),sQuery(id+"F0.wireOp",EDGE,"E378"),sQuery(id+"F0.wireOp",EDGE,"E379"),sQuery(id+"F0.wireOp",EDGE,"E380"),sQuery(id+"F0.wireOp",EDGE,"E381"),sQuery(id+"F0.wireOp",EDGE,"E382"),sQuery(id+"F0.wireOp",EDGE,"E384"),sQuery(id+"F0.wireOp",EDGE,"E385"),sQuery(id+"F0.wireOp",EDGE,"E386"),sQuery(id+"F0.wireOp",EDGE,"E387"),sQuery(id+"F0.wireOp",EDGE,"E388"),sQuery(id+"F0.wireOp",EDGE,"E389"),sQuery(id+"F0.wireOp",EDGE,"E390"),sQuery(id+"F0.wireOp",EDGE,"E391"),sQuery(id+"F0.wireOp",EDGE,"E392"),sQuery(id+"F0.wireOp",EDGE,"E393"),sQuery(id+"F0.wireOp",EDGE,"E394"),sQuery(id+"F0.wireOp",EDGE,"E395"),sQuery(id+"F0.wireOp",EDGE,"E396"),sQuery(id+"F0.wireOp",EDGE,"E397"),sQuery(id+"F0.wireOp",EDGE,"E398"),sQuery(id+"F0.wireOp",EDGE,"E399"),sQuery(id+"F0.wireOp",EDGE,"E400"),sQuery(id+"F0.wireOp",EDGE,"E401"),sQuery(id+"F0.wireOp",EDGE,"E402"),sQuery(id+"F0.wireOp",EDGE,"E403"),sQuery(id+"F0.wireOp",EDGE,"E404"),sQuery(id+"F0.wireOp",EDGE,"E405"),sQuery(id+"F0.wireOp",EDGE,"E406"),sQuery(id+"F0.wireOp",EDGE,"E407"),sQuery(id+"F0.wireOp",EDGE,"E408"),sQuery(id+"F0.wireOp",EDGE,"E409"),sQuery(id+"F0.wireOp",EDGE,"E410"),sQuery(id+"F0.wireOp",EDGE,"E411"),sQuery(id+"F0.wireOp",EDGE,"E412"),sQuery(id+"F0.wireOp",EDGE,"E413"),sQuery(id+"F0.wireOp",EDGE,"E414"),sQuery(id+"F0.wireOp",EDGE,"E415"),sQuery(id+"F0.wireOp",EDGE,"E416"),sQuery(id+"F0.wireOp",EDGE,"E417"),sQuery(id+"F0.wireOp",EDGE,"E418"),sQuery(id+"F0.wireOp",EDGE,"E419"),sQuery(id+"F0.wireOp",EDGE,"E420"),sQuery(id+"F0.wireOp",EDGE,"E421"),sQuery(id+"F0.wireOp",EDGE,"E422"),sQuery(id+"F0.wireOp",EDGE,"E423"),sQuery(id+"F0.wireOp",EDGE,"E424"),sQuery(id+"F0.wireOp",EDGE,"E425"),sQuery(id+"F0.wireOp",EDGE,"E426"),sQuery(id+"F0.wireOp",EDGE,"E427"),sQuery(id+"F0.wireOp",EDGE,"E428"),sQuery(id+"F0.wireOp",EDGE,"E430"),sQuery(id+"F0.wireOp",EDGE,"E433"),sQuery(id+"F0.wireOp",EDGE,"E434"),sQuery(id+"F0.wireOp",EDGE,"E436"),sQuery(id+"F0.wireOp",EDGE,"E437"),sQuery(id+"F0.wireOp",EDGE,"E438"),sQuery(id+"F0.wireOp",EDGE,"E439"),sQuery(id+"F0.wireOp",EDGE,"E440"),sQuery(id+"F0.wireOp",EDGE,"E441"),sQuery(id+"F0.wireOp",EDGE,"E442"),sQuery(id+"F0.wireOp",EDGE,"E443"),sQuery(id+"F0.wireOp",EDGE,"E444"),sQuery(id+"F0.wireOp",EDGE,"E445"),sQuery(id+"F0.wireOp",EDGE,"E446"),sQuery(id+"F0.wireOp",EDGE,"E447"),sQuery(id+"F0.wireOp",EDGE,"E448"),sQuery(id+"F0.wireOp",EDGE,"E449"),sQuery(id+"F0.wireOp",EDGE,"E453"),sQuery(id+"F0.wireOp",EDGE,"E454"),sQuery(id+"F0.wireOp",EDGE,"E455"),sQuery(id+"F0.wireOp",EDGE,"E457"),sQuery(id+"F0.wireOp",EDGE,"E458"),sQuery(id+"F0.wireOp",EDGE,"E459"),sQuery(id+"F0.wireOp",EDGE,"E460"),sQuery(id+"F0.wireOp",EDGE,"E461"),sQuery(id+"F0.wireOp",EDGE,"E462"),sQuery(id+"F0.wireOp",EDGE,"E463"),sQuery(id+"F0.wireOp",EDGE,"E464"),sQuery(id+"F0.wireOp",EDGE,"E465"),sQuery(id+"F0.wireOp",EDGE,"E466"),sQuery(id+"F0.wireOp",EDGE,"E467"),sQuery(id+"F0.wireOp",EDGE,"E468"),sQuery(id+"F0.wireOp",EDGE,"E469"),sQuery(id+"F0.wireOp",EDGE,"E470"),sQuery(id+"F0.wireOp",EDGE,"E471"),sQuery(id+"F0.wireOp",EDGE,"E472"),sQuery(id+"F0.wireOp",EDGE,"E473"),sQuery(id+"F0.wireOp",EDGE,"E474"),sQuery(id+"F0.wireOp",EDGE,"E475"),sQuery(id+"F0.wireOp",EDGE,"E476"),sQuery(id+"F0.wireOp",EDGE,"E477"),sQuery(id+"F0.wireOp",EDGE,"E478"),sQuery(id+"F0.wireOp",EDGE,"E479"),sQuery(id+"F0.wireOp",EDGE,"E480"),sQuery(id+"F0.wireOp",EDGE,"E481"),sQuery(id+"F0.wireOp",EDGE,"E482"),sQuery(id+"F0.wireOp",EDGE,"E483"),sQuery(id+"F0.wireOp",EDGE,"E484"),sQuery(id+"F0.wireOp",EDGE,"E485"),sQuery(id+"F0.wireOp",EDGE,"E486"),sQuery(id+"F0.wireOp",EDGE,"E487"),sQuery(id+"F0.wireOp",EDGE,"E488"),sQuery(id+"F0.wireOp",EDGE,"E489"),sQuery(id+"F0.wireOp",EDGE,"E490"),sQuery(id+"F0.wireOp",EDGE,"E491"),sQuery(id+"F0.wireOp",EDGE,"E492"),sQuery(id+"F0.wireOp",EDGE,"E493"),sQuery(id+"F0.wireOp",EDGE,"E495"),sQuery(id+"F0.wireOp",EDGE,"E496"),sQuery(id+"F0.wireOp",EDGE,"E497"),sQuery(id+"F0.wireOp",EDGE,"E498"),sQuery(id+"F0.wireOp",EDGE,"E499"),sQuery(id+"F0.wireOp",EDGE,"E500"),sQuery(id+"F0.wireOp",EDGE,"E501"),sQuery(id+"F0.wireOp",EDGE,"E502"),sQuery(id+"F0.wireOp",EDGE,"E503"),sQuery(id+"F0.wireOp",EDGE,"E504"),sQuery(id+"F0.wireOp",EDGE,"E505"),sQuery(id+"F0.wireOp",EDGE,"E506"),sQuery(id+"F0.wireOp",EDGE,"E507"),sQuery(id+"F0.wireOp",EDGE,"E508"),sQuery(id+"F0.wireOp",EDGE,"E509"),sQuery(id+"F0.wireOp",EDGE,"E510"),sQuery(id+"F0.wireOp",EDGE,"E511"),sQuery(id+"F0.wireOp",EDGE,"E512"),sQuery(id+"F0.wireOp",EDGE,"E513"),sQuery(id+"F0.wireOp",EDGE,"E514"),sQuery(id+"F0.wireOp",EDGE,"E515"),sQuery(id+"F0.wireOp",EDGE,"E516"),sQuery(id+"F0.wireOp",EDGE,"E517"),sQuery(id+"F0.wireOp",EDGE,"E518"),sQuery(id+"F0.wireOp",EDGE,"E519"),sQuery(id+"F0.wireOp",EDGE,"E520"),sQuery(id+"F0.wireOp",EDGE,"E521"),sQuery(id+"F0.wireOp",EDGE,"E522"),sQuery(id+"F0.wireOp",EDGE,"E523"),sQuery(id+"F0.wireOp",EDGE,"E524"),sQuery(id+"F0.wireOp",EDGE,"E525"),sQuery(id+"F0.wireOp",EDGE,"E526"),sQuery(id+"F0.wireOp",EDGE,"E527"),sQuery(id+"F0.wireOp",EDGE,"E528"),sQuery(id+"F0.wireOp",EDGE,"E529"),sQuery(id+"F0.wireOp",EDGE,"E530"),sQuery(id+"F0.wireOp",EDGE,"E531"),sQuery(id+"F0.wireOp",EDGE,"E532"),sQuery(id+"F0.wireOp",EDGE,"E533"),sQuery(id+"F0.wireOp",EDGE,"E534"),sQuery(id+"F0.wireOp",EDGE,"E535"),sQuery(id+"F0.wireOp",EDGE,"E536"),sQuery(id+"F0.wireOp",EDGE,"E537"),sQuery(id+"F0.wireOp",EDGE,"E538"),sQuery(id+"F0.wireOp",EDGE,"E539"),sQuery(id+"F0.wireOp",EDGE,"E540"),sQuery(id+"F0.wireOp",EDGE,"E541"),sQuery(id+"F0.wireOp",EDGE,"E542"),sQuery(id+"F0.wireOp",EDGE,"E543"),sQuery(id+"F0.wireOp",EDGE,"E544"),sQuery(id+"F0.wireOp",EDGE,"E545"),sQuery(id+"F0.wireOp",EDGE,"E549"),sQuery(id+"F0.wireOp",EDGE,"E550"),sQuery(id+"F0.wireOp",EDGE,"E551"),sQuery(id+"F0.wireOp",EDGE,"E552"),sQuery(id+"F0.wireOp",EDGE,"E553"),sQuery(id+"F0.wireOp",EDGE,"E555"),sQuery(id+"F0.wireOp",EDGE,"E556"),sQuery(id+"F0.wireOp",EDGE,"E557"),sQuery(id+"F0.wireOp",EDGE,"E558"),sQuery(id+"F0.wireOp",EDGE,"E559"),sQuery(id+"F0.wireOp",EDGE,"E560"),sQuery(id+"F0.wireOp",EDGE,"E561"),sQuery(id+"F0.wireOp",EDGE,"E562"),sQuery(id+"F0.wireOp",EDGE,"E563"),sQuery(id+"F0.wireOp",EDGE,"E565"),sQuery(id+"F0.wireOp",EDGE,"E566"),sQuery(id+"F0.wireOp",EDGE,"E567"),sQuery(id+"F0.wireOp",EDGE,"E568"),sQuery(id+"F0.wireOp",EDGE,"E569"),sQuery(id+"F0.wireOp",EDGE,"E570"),sQuery(id+"F0.wireOp",EDGE,"E571"),sQuery(id+"F0.wireOp",EDGE,"E572"),sQuery(id+"F0.wireOp",EDGE,"E573"),sQuery(id+"F0.wireOp",EDGE,"E575"),sQuery(id+"F0.wireOp",EDGE,"E576"),sQuery(id+"F0.wireOp",EDGE,"E577"),sQuery(id+"F0.wireOp",EDGE,"E579"),sQuery(id+"F0.wireOp",EDGE,"E580"),sQuery(id+"F0.wireOp",EDGE,"E581"),sQuery(id+"F0.wireOp",EDGE,"E582"),sQuery(id+"F0.wireOp",EDGE,"E583"),sQuery(id+"F0.wireOp",EDGE,"E584"),sQuery(id+"F0.wireOp",EDGE,"E585"),sQuery(id+"F0.wireOp",EDGE,"E586"),sQuery(id+"F0.wireOp",EDGE,"E587"),sQuery(id+"F0.wireOp",EDGE,"E588"),sQuery(id+"F0.wireOp",EDGE,"E589"),sQuery(id+"F0.wireOp",EDGE,"E591"),sQuery(id+"F0.wireOp",EDGE,"E592"),sQuery(id+"F0.wireOp",EDGE,"E593"),sQuery(id+"F0.wireOp",EDGE,"E594"),sQuery(id+"F0.wireOp",EDGE,"E595"),sQuery(id+"F0.wireOp",EDGE,"E596"),sQuery(id+"F0.wireOp",EDGE,"E597"),sQuery(id+"F0.wireOp",EDGE,"E598"),sQuery(id+"F0.wireOp",EDGE,"E599"),sQuery(id+"F0.wireOp",EDGE,"E600"),sQuery(id+"F0.wireOp",EDGE,"E601"),sQuery(id+"F0.wireOp",EDGE,"E602"),sQuery(id+"F0.wireOp",EDGE,"E603"),sQuery(id+"F0.wireOp",EDGE,"E604"),sQuery(id+"F0.wireOp",EDGE,"E605"),sQuery(id+"F0.wireOp",EDGE,"E606"),sQuery(id+"F0.wireOp",EDGE,"E607"),sQuery(id+"F0.wireOp",EDGE,"E608"),sQuery(id+"F0.wireOp",EDGE,"E609"),sQuery(id+"F0.wireOp",EDGE,"E610"),sQuery(id+"F0.wireOp",EDGE,"E611"),sQuery(id+"F0.wireOp",EDGE,"E612"),sQuery(id+"F0.wireOp",EDGE,"E613"),sQuery(id+"F0.wireOp",EDGE,"E614"),sQuery(id+"F0.wireOp",EDGE,"E615"),sQuery(id+"F0.wireOp",EDGE,"E616"),sQuery(id+"F0.wireOp",EDGE,"E617"),sQuery(id+"F0.wireOp",EDGE,"E619"),sQuery(id+"F0.wireOp",EDGE,"E620"),sQuery(id+"F0.wireOp",EDGE,"E621"),sQuery(id+"F0.wireOp",EDGE,"E622"),sQuery(id+"F0.wireOp",EDGE,"E623"),sQuery(id+"F0.wireOp",EDGE,"E624"),sQuery(id+"F0.wireOp",EDGE,"E625"),sQuery(id+"F0.wireOp",EDGE,"E626"),sQuery(id+"F0.wireOp",EDGE,"E627"),sQuery(id+"F0.wireOp",EDGE,"E628"),sQuery(id+"F0.wireOp",EDGE,"E629"),sQuery(id+"F0.wireOp",EDGE,"E630"),sQuery(id+"F0.wireOp",EDGE,"E631"),sQuery(id+"F0.wireOp",EDGE,"E632"),sQuery(id+"F0.wireOp",EDGE,"E633"),sQuery(id+"F0.wireOp",EDGE,"E634"),sQuery(id+"F0.wireOp",EDGE,"E635"),sQuery(id+"F0.wireOp",EDGE,"E636"),sQuery(id+"F0.wireOp",EDGE,"E637"),sQuery(id+"F0.wireOp",EDGE,"E638"),sQuery(id+"F0.wireOp",EDGE,"E639"),sQuery(id+"F0.wireOp",EDGE,"E640"),sQuery(id+"F0.wireOp",EDGE,"E641")])],"isStart":false});
            var sketch = newSketch(context, id + "F2", { "sketchPlane" : qUnion([Q0])});
            skLineSegment(sketch, "E644", {"start": v(-78.7, -74.49) * mm, "end": v(61.3, -74.49) * mm});
            skLineSegment(sketch, "E645", {"start": v(61.3, -74.49) * mm, "end": v(61.3, -80.49) * mm});
            skLineSegment(sketch, "E646", {"start": v(61.3, -80.49) * mm, "end": v(-78.7, -80.49) * mm});
            skLineSegment(sketch, "E647", {"start": v(-78.7, -80.49) * mm, "end": v(-78.7, -74.49) * mm});
            skLineSegment(sketch, "E648", {"start": v(-58.7, -80.49) * mm, "end": v(-51.2, -130.49) * mm});
            skLineSegment(sketch, "E649", {"start": v(-51.2, -130.49) * mm, "end": v(-43.7, -80.49) * mm});
            skLineSegment(sketch, "E650", {"start": v(26.3, -80.49) * mm, "end": v(33.8, -132.62) * mm});
            skLineSegment(sketch, "E651", {"start": v(33.8, -132.62) * mm, "end": v(41.3, -80.49) * mm});
            skSolve(sketch);
        }
        {
            var Q0;
            {var subQ8=sQuery(id+"F2.wireOp",EDGE,"E645");Q0=makeQuery(id+"F2.imprint","IMPRINT",FACE,{"disambiguationData":[TD([[makeQuery(id+"F2.imprint","IMPRINT",EDGE,{"derivedFrom":subQ8}),-1.0]])]});}
            var Q1;
            {var subQ0=sQuery(id+"F2.wireOp",EDGE,"E648");Q1=makeQuery(id+"F2.imprint","IMPRINT",FACE,{"disambiguationData":[TD([[makeQuery(id+"F2.imprint","IMPRINT",EDGE,{"derivedFrom":subQ0}),1.0]])]});}
            var Q2;
            {var subQ0=sQuery(id+"F2.wireOp",EDGE,"E650");Q2=makeQuery(id+"F2.imprint","IMPRINT",FACE,{"disambiguationData":[TD([[makeQuery(id+"F2.imprint","IMPRINT",EDGE,{"derivedFrom":subQ0}),1.0]])]});}
            var Q3;
            Q3=makeQuery(id+"F1.opExtrude","CAP_FACE",FACE,{"disambiguationData":[OSD([sQuery(id+"F0.wireOp",EDGE,"E0"),sQuery(id+"F0.wireOp",EDGE,"E1"),sQuery(id+"F0.wireOp",EDGE,"E2"),sQuery(id+"F0.wireOp",EDGE,"E3"),sQuery(id+"F0.wireOp",EDGE,"E4"),sQuery(id+"F0.wireOp",EDGE,"E5"),sQuery(id+"F0.wireOp",EDGE,"E6"),sQuery(id+"F0.wireOp",EDGE,"E7"),sQuery(id+"F0.wireOp",EDGE,"E8"),sQuery(id+"F0.wireOp",EDGE,"E9"),sQuery(id+"F0.wireOp",EDGE,"E10"),sQuery(id+"F0.wireOp",EDGE,"E11"),sQuery(id+"F0.wireOp",EDGE,"E12"),sQuery(id+"F0.wireOp",EDGE,"E13"),sQuery(id+"F0.wireOp",EDGE,"E14"),sQuery(id+"F0.wireOp",EDGE,"E15"),sQuery(id+"F0.wireOp",EDGE,"E16"),sQuery(id+"F0.wireOp",EDGE,"E17"),sQuery(id+"F0.wireOp",EDGE,"E18"),sQuery(id+"F0.wireOp",EDGE,"E19"),sQuery(id+"F0.wireOp",EDGE,"E20"),sQuery(id+"F0.wireOp",EDGE,"E21"),sQuery(id+"F0.wireOp",EDGE,"E23"),sQuery(id+"F0.wireOp",EDGE,"E24"),sQuery(id+"F0.wireOp",EDGE,"E25"),sQuery(id+"F0.wireOp",EDGE,"E26"),sQuery(id+"F0.wireOp",EDGE,"E27"),sQuery(id+"F0.wireOp",EDGE,"E28"),sQuery(id+"F0.wireOp",EDGE,"E29"),sQuery(id+"F0.wireOp",EDGE,"E30"),sQuery(id+"F0.wireOp",EDGE,"E31"),sQuery(id+"F0.wireOp",EDGE,"E32"),sQuery(id+"F0.wireOp",EDGE,"E33"),sQuery(id+"F0.wireOp",EDGE,"E34"),sQuery(id+"F0.wireOp",EDGE,"E35"),sQuery(id+"F0.wireOp",EDGE,"E36"),sQuery(id+"F0.wireOp",EDGE,"E37"),sQuery(id+"F0.wireOp",EDGE,"E38"),sQuery(id+"F0.wireOp",EDGE,"E39"),sQuery(id+"F0.wireOp",EDGE,"E40"),sQuery(id+"F0.wireOp",EDGE,"E41"),sQuery(id+"F0.wireOp",EDGE,"E42"),sQuery(id+"F0.wireOp",EDGE,"E43"),sQuery(id+"F0.wireOp",EDGE,"E44"),sQuery(id+"F0.wireOp",EDGE,"E45"),sQuery(id+"F0.wireOp",EDGE,"E46"),sQuery(id+"F0.wireOp",EDGE,"E47"),sQuery(id+"F0.wireOp",EDGE,"E48"),sQuery(id+"F0.wireOp",EDGE,"E49"),sQuery(id+"F0.wireOp",EDGE,"E50"),sQuery(id+"F0.wireOp",EDGE,"E51"),sQuery(id+"F0.wireOp",EDGE,"E53"),sQuery(id+"F0.wireOp",EDGE,"E54"),sQuery(id+"F0.wireOp",EDGE,"E55"),sQuery(id+"F0.wireOp",EDGE,"E56"),sQuery(id+"F0.wireOp",EDGE,"E58"),sQuery(id+"F0.wireOp",EDGE,"E59"),sQuery(id+"F0.wireOp",EDGE,"E60"),sQuery(id+"F0.wireOp",EDGE,"E61"),sQuery(id+"F0.wireOp",EDGE,"E62"),sQuery(id+"F0.wireOp",EDGE,"E63"),sQuery(id+"F0.wireOp",EDGE,"E64"),sQuery(id+"F0.wireOp",EDGE,"E65"),sQuery(id+"F0.wireOp",EDGE,"E66"),sQuery(id+"F0.wireOp",EDGE,"E67"),sQuery(id+"F0.wireOp",EDGE,"E68"),sQuery(id+"F0.wireOp",EDGE,"E69"),sQuery(id+"F0.wireOp",EDGE,"E70"),sQuery(id+"F0.wireOp",EDGE,"E71"),sQuery(id+"F0.wireOp",EDGE,"E72"),sQuery(id+"F0.wireOp",EDGE,"E73"),sQuery(id+"F0.wireOp",EDGE,"E74"),sQuery(id+"F0.wireOp",EDGE,"E75"),sQuery(id+"F0.wireOp",EDGE,"E76"),sQuery(id+"F0.wireOp",EDGE,"E77"),sQuery(id+"F0.wireOp",EDGE,"E78"),sQuery(id+"F0.wireOp",EDGE,"E79"),sQuery(id+"F0.wireOp",EDGE,"E80"),sQuery(id+"F0.wireOp",EDGE,"E81"),sQuery(id+"F0.wireOp",EDGE,"E82"),sQuery(id+"F0.wireOp",EDGE,"E83"),sQuery(id+"F0.wireOp",EDGE,"E84"),sQuery(id+"F0.wireOp",EDGE,"E85"),sQuery(id+"F0.wireOp",EDGE,"E86"),sQuery(id+"F0.wireOp",EDGE,"E88"),sQuery(id+"F0.wireOp",EDGE,"E89"),sQuery(id+"F0.wireOp",EDGE,"E90"),sQuery(id+"F0.wireOp",EDGE,"E91"),sQuery(id+"F0.wireOp",EDGE,"E92"),sQuery(id+"F0.wireOp",EDGE,"E93"),sQuery(id+"F0.wireOp",EDGE,"E94"),sQuery(id+"F0.wireOp",EDGE,"E95"),sQuery(id+"F0.wireOp",EDGE,"E96"),sQuery(id+"F0.wireOp",EDGE,"E97"),sQuery(id+"F0.wireOp",EDGE,"E98"),sQuery(id+"F0.wireOp",EDGE,"E99"),sQuery(id+"F0.wireOp",EDGE,"E100"),sQuery(id+"F0.wireOp",EDGE,"E101"),sQuery(id+"F0.wireOp",EDGE,"E104"),sQuery(id+"F0.wireOp",EDGE,"E105"),sQuery(id+"F0.wireOp",EDGE,"E106"),sQuery(id+"F0.wireOp",EDGE,"E107"),sQuery(id+"F0.wireOp",EDGE,"E108"),sQuery(id+"F0.wireOp",EDGE,"E109"),sQuery(id+"F0.wireOp",EDGE,"E110"),sQuery(id+"F0.wireOp",EDGE,"E112"),sQuery(id+"F0.wireOp",EDGE,"E113"),sQuery(id+"F0.wireOp",EDGE,"E114"),sQuery(id+"F0.wireOp",EDGE,"E115"),sQuery(id+"F0.wireOp",EDGE,"E116"),sQuery(id+"F0.wireOp",EDGE,"E117"),sQuery(id+"F0.wireOp",EDGE,"E118"),sQuery(id+"F0.wireOp",EDGE,"E119"),sQuery(id+"F0.wireOp",EDGE,"E120"),sQuery(id+"F0.wireOp",EDGE,"E121"),sQuery(id+"F0.wireOp",EDGE,"E122"),sQuery(id+"F0.wireOp",EDGE,"E123"),sQuery(id+"F0.wireOp",EDGE,"E124"),sQuery(id+"F0.wireOp",EDGE,"E125"),sQuery(id+"F0.wireOp",EDGE,"E126"),sQuery(id+"F0.wireOp",EDGE,"E127"),sQuery(id+"F0.wireOp",EDGE,"E128"),sQuery(id+"F0.wireOp",EDGE,"E129"),sQuery(id+"F0.wireOp",EDGE,"E130"),sQuery(id+"F0.wireOp",EDGE,"E131"),sQuery(id+"F0.wireOp",EDGE,"E132"),sQuery(id+"F0.wireOp",EDGE,"E133"),sQuery(id+"F0.wireOp",EDGE,"E134"),sQuery(id+"F0.wireOp",EDGE,"E135"),sQuery(id+"F0.wireOp",EDGE,"E136"),sQuery(id+"F0.wireOp",EDGE,"E137"),sQuery(id+"F0.wireOp",EDGE,"E138"),sQuery(id+"F0.wireOp",EDGE,"E139"),sQuery(id+"F0.wireOp",EDGE,"E140"),sQuery(id+"F0.wireOp",EDGE,"E141"),sQuery(id+"F0.wireOp",EDGE,"E142"),sQuery(id+"F0.wireOp",EDGE,"E143"),sQuery(id+"F0.wireOp",EDGE,"E144"),sQuery(id+"F0.wireOp",EDGE,"E145"),sQuery(id+"F0.wireOp",EDGE,"E146"),sQuery(id+"F0.wireOp",EDGE,"E147"),sQuery(id+"F0.wireOp",EDGE,"E148"),sQuery(id+"F0.wireOp",EDGE,"E149"),sQuery(id+"F0.wireOp",EDGE,"E150"),sQuery(id+"F0.wireOp",EDGE,"E151"),sQuery(id+"F0.wireOp",EDGE,"E152"),sQuery(id+"F0.wireOp",EDGE,"E153"),sQuery(id+"F0.wireOp",EDGE,"E154"),sQuery(id+"F0.wireOp",EDGE,"E155"),sQuery(id+"F0.wireOp",EDGE,"E156"),sQuery(id+"F0.wireOp",EDGE,"E158"),sQuery(id+"F0.wireOp",EDGE,"E159"),sQuery(id+"F0.wireOp",EDGE,"E160"),sQuery(id+"F0.wireOp",EDGE,"E161"),sQuery(id+"F0.wireOp",EDGE,"E162"),sQuery(id+"F0.wireOp",EDGE,"E163"),sQuery(id+"F0.wireOp",EDGE,"E164"),sQuery(id+"F0.wireOp",EDGE,"E165"),sQuery(id+"F0.wireOp",EDGE,"E166"),sQuery(id+"F0.wireOp",EDGE,"E167"),sQuery(id+"F0.wireOp",EDGE,"E168"),sQuery(id+"F0.wireOp",EDGE,"E169"),sQuery(id+"F0.wireOp",EDGE,"E170"),sQuery(id+"F0.wireOp",EDGE,"E171"),sQuery(id+"F0.wireOp",EDGE,"E172"),sQuery(id+"F0.wireOp",EDGE,"E173"),sQuery(id+"F0.wireOp",EDGE,"E174"),sQuery(id+"F0.wireOp",EDGE,"E175"),sQuery(id+"F0.wireOp",EDGE,"E176"),sQuery(id+"F0.wireOp",EDGE,"E177"),sQuery(id+"F0.wireOp",EDGE,"E178"),sQuery(id+"F0.wireOp",EDGE,"E179"),sQuery(id+"F0.wireOp",EDGE,"E180"),sQuery(id+"F0.wireOp",EDGE,"E181"),sQuery(id+"F0.wireOp",EDGE,"E182"),sQuery(id+"F0.wireOp",EDGE,"E183"),sQuery(id+"F0.wireOp",EDGE,"E184"),sQuery(id+"F0.wireOp",EDGE,"E185"),sQuery(id+"F0.wireOp",EDGE,"E186"),sQuery(id+"F0.wireOp",EDGE,"E187"),sQuery(id+"F0.wireOp",EDGE,"E188"),sQuery(id+"F0.wireOp",EDGE,"E189"),sQuery(id+"F0.wireOp",EDGE,"E190"),sQuery(id+"F0.wireOp",EDGE,"E191"),sQuery(id+"F0.wireOp",EDGE,"E198"),sQuery(id+"F0.wireOp",EDGE,"E199"),sQuery(id+"F0.wireOp",EDGE,"E200"),sQuery(id+"F0.wireOp",EDGE,"E201"),sQuery(id+"F0.wireOp",EDGE,"E202"),sQuery(id+"F0.wireOp",EDGE,"E203"),sQuery(id+"F0.wireOp",EDGE,"E204"),sQuery(id+"F0.wireOp",EDGE,"E205"),sQuery(id+"F0.wireOp",EDGE,"E206"),sQuery(id+"F0.wireOp",EDGE,"E207"),sQuery(id+"F0.wireOp",EDGE,"E208"),sQuery(id+"F0.wireOp",EDGE,"E209"),sQuery(id+"F0.wireOp",EDGE,"E210"),sQuery(id+"F0.wireOp",EDGE,"E211"),sQuery(id+"F0.wireOp",EDGE,"E212"),sQuery(id+"F0.wireOp",EDGE,"E213"),sQuery(id+"F0.wireOp",EDGE,"E215"),sQuery(id+"F0.wireOp",EDGE,"E216"),sQuery(id+"F0.wireOp",EDGE,"E217"),sQuery(id+"F0.wireOp",EDGE,"E218"),sQuery(id+"F0.wireOp",EDGE,"E219"),sQuery(id+"F0.wireOp",EDGE,"E220"),sQuery(id+"F0.wireOp",EDGE,"E221"),sQuery(id+"F0.wireOp",EDGE,"E222"),sQuery(id+"F0.wireOp",EDGE,"E224"),sQuery(id+"F0.wireOp",EDGE,"E225"),sQuery(id+"F0.wireOp",EDGE,"E226"),sQuery(id+"F0.wireOp",EDGE,"E227"),sQuery(id+"F0.wireOp",EDGE,"E228"),sQuery(id+"F0.wireOp",EDGE,"E229"),sQuery(id+"F0.wireOp",EDGE,"E230"),sQuery(id+"F0.wireOp",EDGE,"E231"),sQuery(id+"F0.wireOp",EDGE,"E232"),sQuery(id+"F0.wireOp",EDGE,"E233"),sQuery(id+"F0.wireOp",EDGE,"E234"),sQuery(id+"F0.wireOp",EDGE,"E235"),sQuery(id+"F0.wireOp",EDGE,"E236"),sQuery(id+"F0.wireOp",EDGE,"E237"),sQuery(id+"F0.wireOp",EDGE,"E238"),sQuery(id+"F0.wireOp",EDGE,"E239"),sQuery(id+"F0.wireOp",EDGE,"E240"),sQuery(id+"F0.wireOp",EDGE,"E241"),sQuery(id+"F0.wireOp",EDGE,"E242"),sQuery(id+"F0.wireOp",EDGE,"E243"),sQuery(id+"F0.wireOp",EDGE,"E244"),sQuery(id+"F0.wireOp",EDGE,"E245"),sQuery(id+"F0.wireOp",EDGE,"E246"),sQuery(id+"F0.wireOp",EDGE,"E247"),sQuery(id+"F0.wireOp",EDGE,"E248"),sQuery(id+"F0.wireOp",EDGE,"E249"),sQuery(id+"F0.wireOp",EDGE,"E250"),sQuery(id+"F0.wireOp",EDGE,"E251"),sQuery(id+"F0.wireOp",EDGE,"E252"),sQuery(id+"F0.wireOp",EDGE,"E253"),sQuery(id+"F0.wireOp",EDGE,"E254"),sQuery(id+"F0.wireOp",EDGE,"E255"),sQuery(id+"F0.wireOp",EDGE,"E256"),sQuery(id+"F0.wireOp",EDGE,"E257"),sQuery(id+"F0.wireOp",EDGE,"E258"),sQuery(id+"F0.wireOp",EDGE,"E259"),sQuery(id+"F0.wireOp",EDGE,"E260"),sQuery(id+"F0.wireOp",EDGE,"E261"),sQuery(id+"F0.wireOp",EDGE,"E262"),sQuery(id+"F0.wireOp",EDGE,"E263"),sQuery(id+"F0.wireOp",EDGE,"E264"),sQuery(id+"F0.wireOp",EDGE,"E265"),sQuery(id+"F0.wireOp",EDGE,"E266"),sQuery(id+"F0.wireOp",EDGE,"E267"),sQuery(id+"F0.wireOp",EDGE,"E268"),sQuery(id+"F0.wireOp",EDGE,"E269"),sQuery(id+"F0.wireOp",EDGE,"E270"),sQuery(id+"F0.wireOp",EDGE,"E271"),sQuery(id+"F0.wireOp",EDGE,"E273"),sQuery(id+"F0.wireOp",EDGE,"E274"),sQuery(id+"F0.wireOp",EDGE,"E275"),sQuery(id+"F0.wireOp",EDGE,"E276"),sQuery(id+"F0.wireOp",EDGE,"E277"),sQuery(id+"F0.wireOp",EDGE,"E278"),sQuery(id+"F0.wireOp",EDGE,"E279"),sQuery(id+"F0.wireOp",EDGE,"E280"),sQuery(id+"F0.wireOp",EDGE,"E281"),sQuery(id+"F0.wireOp",EDGE,"E282"),sQuery(id+"F0.wireOp",EDGE,"E283"),sQuery(id+"F0.wireOp",EDGE,"E284"),sQuery(id+"F0.wireOp",EDGE,"E285"),sQuery(id+"F0.wireOp",EDGE,"E286"),sQuery(id+"F0.wireOp",EDGE,"E287"),sQuery(id+"F0.wireOp",EDGE,"E288"),sQuery(id+"F0.wireOp",EDGE,"E289"),sQuery(id+"F0.wireOp",EDGE,"E290"),sQuery(id+"F0.wireOp",EDGE,"E291"),sQuery(id+"F0.wireOp",EDGE,"E293"),sQuery(id+"F0.wireOp",EDGE,"E294"),sQuery(id+"F0.wireOp",EDGE,"E296"),sQuery(id+"F0.wireOp",EDGE,"E297"),sQuery(id+"F0.wireOp",EDGE,"E298"),sQuery(id+"F0.wireOp",EDGE,"E299"),sQuery(id+"F0.wireOp",EDGE,"E300"),sQuery(id+"F0.wireOp",EDGE,"E301"),sQuery(id+"F0.wireOp",EDGE,"E302"),sQuery(id+"F0.wireOp",EDGE,"E303"),sQuery(id+"F0.wireOp",EDGE,"E304"),sQuery(id+"F0.wireOp",EDGE,"E305"),sQuery(id+"F0.wireOp",EDGE,"E306"),sQuery(id+"F0.wireOp",EDGE,"E307"),sQuery(id+"F0.wireOp",EDGE,"E308"),sQuery(id+"F0.wireOp",EDGE,"E309"),sQuery(id+"F0.wireOp",EDGE,"E310"),sQuery(id+"F0.wireOp",EDGE,"E311"),sQuery(id+"F0.wireOp",EDGE,"E312"),sQuery(id+"F0.wireOp",EDGE,"E313"),sQuery(id+"F0.wireOp",EDGE,"E314"),sQuery(id+"F0.wireOp",EDGE,"E315"),sQuery(id+"F0.wireOp",EDGE,"E316"),sQuery(id+"F0.wireOp",EDGE,"E317"),sQuery(id+"F0.wireOp",EDGE,"E318"),sQuery(id+"F0.wireOp",EDGE,"E320"),sQuery(id+"F0.wireOp",EDGE,"E321"),sQuery(id+"F0.wireOp",EDGE,"E322"),sQuery(id+"F0.wireOp",EDGE,"E327"),sQuery(id+"F0.wireOp",EDGE,"E328"),sQuery(id+"F0.wireOp",EDGE,"E329"),sQuery(id+"F0.wireOp",EDGE,"E330"),sQuery(id+"F0.wireOp",EDGE,"E331"),sQuery(id+"F0.wireOp",EDGE,"E332"),sQuery(id+"F0.wireOp",EDGE,"E333"),sQuery(id+"F0.wireOp",EDGE,"E334"),sQuery(id+"F0.wireOp",EDGE,"E335"),sQuery(id+"F0.wireOp",EDGE,"E336"),sQuery(id+"F0.wireOp",EDGE,"E337"),sQuery(id+"F0.wireOp",EDGE,"E338"),sQuery(id+"F0.wireOp",EDGE,"E339"),sQuery(id+"F0.wireOp",EDGE,"E340"),sQuery(id+"F0.wireOp",EDGE,"E341"),sQuery(id+"F0.wireOp",EDGE,"E342"),sQuery(id+"F0.wireOp",EDGE,"E343"),sQuery(id+"F0.wireOp",EDGE,"E344"),sQuery(id+"F0.wireOp",EDGE,"E345"),sQuery(id+"F0.wireOp",EDGE,"E346"),sQuery(id+"F0.wireOp",EDGE,"E347"),sQuery(id+"F0.wireOp",EDGE,"E348"),sQuery(id+"F0.wireOp",EDGE,"E349"),sQuery(id+"F0.wireOp",EDGE,"E350"),sQuery(id+"F0.wireOp",EDGE,"E351"),sQuery(id+"F0.wireOp",EDGE,"E353"),sQuery(id+"F0.wireOp",EDGE,"E354"),sQuery(id+"F0.wireOp",EDGE,"E355"),sQuery(id+"F0.wireOp",EDGE,"E356"),sQuery(id+"F0.wireOp",EDGE,"E357"),sQuery(id+"F0.wireOp",EDGE,"E358"),sQuery(id+"F0.wireOp",EDGE,"E359"),sQuery(id+"F0.wireOp",EDGE,"E360"),sQuery(id+"F0.wireOp",EDGE,"E361"),sQuery(id+"F0.wireOp",EDGE,"E362"),sQuery(id+"F0.wireOp",EDGE,"E363"),sQuery(id+"F0.wireOp",EDGE,"E364"),sQuery(id+"F0.wireOp",EDGE,"E365"),sQuery(id+"F0.wireOp",EDGE,"E366"),sQuery(id+"F0.wireOp",EDGE,"E367"),sQuery(id+"F0.wireOp",EDGE,"E368"),sQuery(id+"F0.wireOp",EDGE,"E369"),sQuery(id+"F0.wireOp",EDGE,"E370"),sQuery(id+"F0.wireOp",EDGE,"E371"),sQuery(id+"F0.wireOp",EDGE,"E373"),sQuery(id+"F0.wireOp",EDGE,"E374"),sQuery(id+"F0.wireOp",EDGE,"E375"),sQuery(id+"F0.wireOp",EDGE,"E376"),sQuery(id+"F0.wireOp",EDGE,"E377"),sQuery(id+"F0.wireOp",EDGE,"E378"),sQuery(id+"F0.wireOp",EDGE,"E379"),sQuery(id+"F0.wireOp",EDGE,"E380"),sQuery(id+"F0.wireOp",EDGE,"E381"),sQuery(id+"F0.wireOp",EDGE,"E382"),sQuery(id+"F0.wireOp",EDGE,"E384"),sQuery(id+"F0.wireOp",EDGE,"E385"),sQuery(id+"F0.wireOp",EDGE,"E386"),sQuery(id+"F0.wireOp",EDGE,"E387"),sQuery(id+"F0.wireOp",EDGE,"E388"),sQuery(id+"F0.wireOp",EDGE,"E389"),sQuery(id+"F0.wireOp",EDGE,"E390"),sQuery(id+"F0.wireOp",EDGE,"E391"),sQuery(id+"F0.wireOp",EDGE,"E392"),sQuery(id+"F0.wireOp",EDGE,"E393"),sQuery(id+"F0.wireOp",EDGE,"E394"),sQuery(id+"F0.wireOp",EDGE,"E395"),sQuery(id+"F0.wireOp",EDGE,"E396"),sQuery(id+"F0.wireOp",EDGE,"E397"),sQuery(id+"F0.wireOp",EDGE,"E398"),sQuery(id+"F0.wireOp",EDGE,"E399"),sQuery(id+"F0.wireOp",EDGE,"E400"),sQuery(id+"F0.wireOp",EDGE,"E401"),sQuery(id+"F0.wireOp",EDGE,"E402"),sQuery(id+"F0.wireOp",EDGE,"E403"),sQuery(id+"F0.wireOp",EDGE,"E404"),sQuery(id+"F0.wireOp",EDGE,"E405"),sQuery(id+"F0.wireOp",EDGE,"E406"),sQuery(id+"F0.wireOp",EDGE,"E407"),sQuery(id+"F0.wireOp",EDGE,"E408"),sQuery(id+"F0.wireOp",EDGE,"E409"),sQuery(id+"F0.wireOp",EDGE,"E410"),sQuery(id+"F0.wireOp",EDGE,"E411"),sQuery(id+"F0.wireOp",EDGE,"E412"),sQuery(id+"F0.wireOp",EDGE,"E413"),sQuery(id+"F0.wireOp",EDGE,"E414"),sQuery(id+"F0.wireOp",EDGE,"E415"),sQuery(id+"F0.wireOp",EDGE,"E416"),sQuery(id+"F0.wireOp",EDGE,"E417"),sQuery(id+"F0.wireOp",EDGE,"E418"),sQuery(id+"F0.wireOp",EDGE,"E419"),sQuery(id+"F0.wireOp",EDGE,"E420"),sQuery(id+"F0.wireOp",EDGE,"E421"),sQuery(id+"F0.wireOp",EDGE,"E422"),sQuery(id+"F0.wireOp",EDGE,"E423"),sQuery(id+"F0.wireOp",EDGE,"E424"),sQuery(id+"F0.wireOp",EDGE,"E425"),sQuery(id+"F0.wireOp",EDGE,"E426"),sQuery(id+"F0.wireOp",EDGE,"E427"),sQuery(id+"F0.wireOp",EDGE,"E428"),sQuery(id+"F0.wireOp",EDGE,"E430"),sQuery(id+"F0.wireOp",EDGE,"E433"),sQuery(id+"F0.wireOp",EDGE,"E434"),sQuery(id+"F0.wireOp",EDGE,"E436"),sQuery(id+"F0.wireOp",EDGE,"E437"),sQuery(id+"F0.wireOp",EDGE,"E438"),sQuery(id+"F0.wireOp",EDGE,"E439"),sQuery(id+"F0.wireOp",EDGE,"E440"),sQuery(id+"F0.wireOp",EDGE,"E441"),sQuery(id+"F0.wireOp",EDGE,"E442"),sQuery(id+"F0.wireOp",EDGE,"E443"),sQuery(id+"F0.wireOp",EDGE,"E444"),sQuery(id+"F0.wireOp",EDGE,"E445"),sQuery(id+"F0.wireOp",EDGE,"E446"),sQuery(id+"F0.wireOp",EDGE,"E447"),sQuery(id+"F0.wireOp",EDGE,"E448"),sQuery(id+"F0.wireOp",EDGE,"E449"),sQuery(id+"F0.wireOp",EDGE,"E453"),sQuery(id+"F0.wireOp",EDGE,"E454"),sQuery(id+"F0.wireOp",EDGE,"E455"),sQuery(id+"F0.wireOp",EDGE,"E457"),sQuery(id+"F0.wireOp",EDGE,"E458"),sQuery(id+"F0.wireOp",EDGE,"E459"),sQuery(id+"F0.wireOp",EDGE,"E460"),sQuery(id+"F0.wireOp",EDGE,"E461"),sQuery(id+"F0.wireOp",EDGE,"E462"),sQuery(id+"F0.wireOp",EDGE,"E463"),sQuery(id+"F0.wireOp",EDGE,"E464"),sQuery(id+"F0.wireOp",EDGE,"E465"),sQuery(id+"F0.wireOp",EDGE,"E466"),sQuery(id+"F0.wireOp",EDGE,"E467"),sQuery(id+"F0.wireOp",EDGE,"E468"),sQuery(id+"F0.wireOp",EDGE,"E469"),sQuery(id+"F0.wireOp",EDGE,"E470"),sQuery(id+"F0.wireOp",EDGE,"E471"),sQuery(id+"F0.wireOp",EDGE,"E472"),sQuery(id+"F0.wireOp",EDGE,"E473"),sQuery(id+"F0.wireOp",EDGE,"E474"),sQuery(id+"F0.wireOp",EDGE,"E475"),sQuery(id+"F0.wireOp",EDGE,"E476"),sQuery(id+"F0.wireOp",EDGE,"E477"),sQuery(id+"F0.wireOp",EDGE,"E478"),sQuery(id+"F0.wireOp",EDGE,"E479"),sQuery(id+"F0.wireOp",EDGE,"E480"),sQuery(id+"F0.wireOp",EDGE,"E481"),sQuery(id+"F0.wireOp",EDGE,"E482"),sQuery(id+"F0.wireOp",EDGE,"E483"),sQuery(id+"F0.wireOp",EDGE,"E484"),sQuery(id+"F0.wireOp",EDGE,"E485"),sQuery(id+"F0.wireOp",EDGE,"E486"),sQuery(id+"F0.wireOp",EDGE,"E487"),sQuery(id+"F0.wireOp",EDGE,"E488"),sQuery(id+"F0.wireOp",EDGE,"E489"),sQuery(id+"F0.wireOp",EDGE,"E490"),sQuery(id+"F0.wireOp",EDGE,"E491"),sQuery(id+"F0.wireOp",EDGE,"E492"),sQuery(id+"F0.wireOp",EDGE,"E493"),sQuery(id+"F0.wireOp",EDGE,"E495"),sQuery(id+"F0.wireOp",EDGE,"E496"),sQuery(id+"F0.wireOp",EDGE,"E497"),sQuery(id+"F0.wireOp",EDGE,"E498"),sQuery(id+"F0.wireOp",EDGE,"E499"),sQuery(id+"F0.wireOp",EDGE,"E500"),sQuery(id+"F0.wireOp",EDGE,"E501"),sQuery(id+"F0.wireOp",EDGE,"E502"),sQuery(id+"F0.wireOp",EDGE,"E503"),sQuery(id+"F0.wireOp",EDGE,"E504"),sQuery(id+"F0.wireOp",EDGE,"E505"),sQuery(id+"F0.wireOp",EDGE,"E506"),sQuery(id+"F0.wireOp",EDGE,"E507"),sQuery(id+"F0.wireOp",EDGE,"E508"),sQuery(id+"F0.wireOp",EDGE,"E509"),sQuery(id+"F0.wireOp",EDGE,"E510"),sQuery(id+"F0.wireOp",EDGE,"E511"),sQuery(id+"F0.wireOp",EDGE,"E512"),sQuery(id+"F0.wireOp",EDGE,"E513"),sQuery(id+"F0.wireOp",EDGE,"E514"),sQuery(id+"F0.wireOp",EDGE,"E515"),sQuery(id+"F0.wireOp",EDGE,"E516"),sQuery(id+"F0.wireOp",EDGE,"E517"),sQuery(id+"F0.wireOp",EDGE,"E518"),sQuery(id+"F0.wireOp",EDGE,"E519"),sQuery(id+"F0.wireOp",EDGE,"E520"),sQuery(id+"F0.wireOp",EDGE,"E521"),sQuery(id+"F0.wireOp",EDGE,"E522"),sQuery(id+"F0.wireOp",EDGE,"E523"),sQuery(id+"F0.wireOp",EDGE,"E524"),sQuery(id+"F0.wireOp",EDGE,"E525"),sQuery(id+"F0.wireOp",EDGE,"E526"),sQuery(id+"F0.wireOp",EDGE,"E527"),sQuery(id+"F0.wireOp",EDGE,"E528"),sQuery(id+"F0.wireOp",EDGE,"E529"),sQuery(id+"F0.wireOp",EDGE,"E530"),sQuery(id+"F0.wireOp",EDGE,"E531"),sQuery(id+"F0.wireOp",EDGE,"E532"),sQuery(id+"F0.wireOp",EDGE,"E533"),sQuery(id+"F0.wireOp",EDGE,"E534"),sQuery(id+"F0.wireOp",EDGE,"E535"),sQuery(id+"F0.wireOp",EDGE,"E536"),sQuery(id+"F0.wireOp",EDGE,"E537"),sQuery(id+"F0.wireOp",EDGE,"E538"),sQuery(id+"F0.wireOp",EDGE,"E539"),sQuery(id+"F0.wireOp",EDGE,"E540"),sQuery(id+"F0.wireOp",EDGE,"E541"),sQuery(id+"F0.wireOp",EDGE,"E542"),sQuery(id+"F0.wireOp",EDGE,"E543"),sQuery(id+"F0.wireOp",EDGE,"E544"),sQuery(id+"F0.wireOp",EDGE,"E545"),sQuery(id+"F0.wireOp",EDGE,"E549"),sQuery(id+"F0.wireOp",EDGE,"E550"),sQuery(id+"F0.wireOp",EDGE,"E551"),sQuery(id+"F0.wireOp",EDGE,"E552"),sQuery(id+"F0.wireOp",EDGE,"E553"),sQuery(id+"F0.wireOp",EDGE,"E555"),sQuery(id+"F0.wireOp",EDGE,"E556"),sQuery(id+"F0.wireOp",EDGE,"E557"),sQuery(id+"F0.wireOp",EDGE,"E558"),sQuery(id+"F0.wireOp",EDGE,"E559"),sQuery(id+"F0.wireOp",EDGE,"E560"),sQuery(id+"F0.wireOp",EDGE,"E561"),sQuery(id+"F0.wireOp",EDGE,"E562"),sQuery(id+"F0.wireOp",EDGE,"E563"),sQuery(id+"F0.wireOp",EDGE,"E565"),sQuery(id+"F0.wireOp",EDGE,"E566"),sQuery(id+"F0.wireOp",EDGE,"E567"),sQuery(id+"F0.wireOp",EDGE,"E568"),sQuery(id+"F0.wireOp",EDGE,"E569"),sQuery(id+"F0.wireOp",EDGE,"E570"),sQuery(id+"F0.wireOp",EDGE,"E571"),sQuery(id+"F0.wireOp",EDGE,"E572"),sQuery(id+"F0.wireOp",EDGE,"E573"),sQuery(id+"F0.wireOp",EDGE,"E575"),sQuery(id+"F0.wireOp",EDGE,"E576"),sQuery(id+"F0.wireOp",EDGE,"E577"),sQuery(id+"F0.wireOp",EDGE,"E579"),sQuery(id+"F0.wireOp",EDGE,"E580"),sQuery(id+"F0.wireOp",EDGE,"E581"),sQuery(id+"F0.wireOp",EDGE,"E582"),sQuery(id+"F0.wireOp",EDGE,"E583"),sQuery(id+"F0.wireOp",EDGE,"E584"),sQuery(id+"F0.wireOp",EDGE,"E585"),sQuery(id+"F0.wireOp",EDGE,"E586"),sQuery(id+"F0.wireOp",EDGE,"E587"),sQuery(id+"F0.wireOp",EDGE,"E588"),sQuery(id+"F0.wireOp",EDGE,"E589"),sQuery(id+"F0.wireOp",EDGE,"E591"),sQuery(id+"F0.wireOp",EDGE,"E592"),sQuery(id+"F0.wireOp",EDGE,"E593"),sQuery(id+"F0.wireOp",EDGE,"E594"),sQuery(id+"F0.wireOp",EDGE,"E595"),sQuery(id+"F0.wireOp",EDGE,"E596"),sQuery(id+"F0.wireOp",EDGE,"E597"),sQuery(id+"F0.wireOp",EDGE,"E598"),sQuery(id+"F0.wireOp",EDGE,"E599"),sQuery(id+"F0.wireOp",EDGE,"E600"),sQuery(id+"F0.wireOp",EDGE,"E601"),sQuery(id+"F0.wireOp",EDGE,"E602"),sQuery(id+"F0.wireOp",EDGE,"E603"),sQuery(id+"F0.wireOp",EDGE,"E604"),sQuery(id+"F0.wireOp",EDGE,"E605"),sQuery(id+"F0.wireOp",EDGE,"E606"),sQuery(id+"F0.wireOp",EDGE,"E607"),sQuery(id+"F0.wireOp",EDGE,"E608"),sQuery(id+"F0.wireOp",EDGE,"E609"),sQuery(id+"F0.wireOp",EDGE,"E610"),sQuery(id+"F0.wireOp",EDGE,"E611"),sQuery(id+"F0.wireOp",EDGE,"E612"),sQuery(id+"F0.wireOp",EDGE,"E613"),sQuery(id+"F0.wireOp",EDGE,"E614"),sQuery(id+"F0.wireOp",EDGE,"E615"),sQuery(id+"F0.wireOp",EDGE,"E616"),sQuery(id+"F0.wireOp",EDGE,"E617"),sQuery(id+"F0.wireOp",EDGE,"E619"),sQuery(id+"F0.wireOp",EDGE,"E620"),sQuery(id+"F0.wireOp",EDGE,"E621"),sQuery(id+"F0.wireOp",EDGE,"E622"),sQuery(id+"F0.wireOp",EDGE,"E623"),sQuery(id+"F0.wireOp",EDGE,"E624"),sQuery(id+"F0.wireOp",EDGE,"E625"),sQuery(id+"F0.wireOp",EDGE,"E626"),sQuery(id+"F0.wireOp",EDGE,"E627"),sQuery(id+"F0.wireOp",EDGE,"E628"),sQuery(id+"F0.wireOp",EDGE,"E629"),sQuery(id+"F0.wireOp",EDGE,"E630"),sQuery(id+"F0.wireOp",EDGE,"E631"),sQuery(id+"F0.wireOp",EDGE,"E632"),sQuery(id+"F0.wireOp",EDGE,"E633"),sQuery(id+"F0.wireOp",EDGE,"E634"),sQuery(id+"F0.wireOp",EDGE,"E635"),sQuery(id+"F0.wireOp",EDGE,"E636"),sQuery(id+"F0.wireOp",EDGE,"E637"),sQuery(id+"F0.wireOp",EDGE,"E638"),sQuery(id+"F0.wireOp",EDGE,"E639"),sQuery(id+"F0.wireOp",EDGE,"E640"),sQuery(id+"F0.wireOp",EDGE,"E641")])],"isStart":true});
            extrude(context, id + "F3", {"entities" : qUnion([Q0, Q1, Q2]), "operationType" : NewBodyOperationType.ADD, "endBound" : BoundingType.UP_TO_SURFACE, "oppositeDirection" : true, "endBoundEntityFace" : qUnion([Q3]), "depth" : 25 * mm});
        }
        {
            var Q0;
            Q0=makeQuery(id+"F3.opExtrude","SWEPT_FACE",FACE,{"disambiguationData":[OSD([sQuery(id+"F2.wireOp",EDGE,"E645")])]});
            var sketch = newSketch(context, id + "F4", { "sketchPlane" : qUnion([Q0])});
            skLineSegment(sketch, "E652.0", {"start": v(0, -132.62) * mm, "end": v(-10, -132.62) * mm});
            skLineSegment(sketch, "E653.0", {"start": v(-10, -132.62) * mm, "end": v(-10, -80.49) * mm});
            skLineSegment(sketch, "E654", {"start": v(-10, -80.49) * mm, "end": v(0, -132.62) * mm});
            skSolve(sketch);
        }
        {
            var Q0;
            Q0=makeQuery(id+"F4.imprint","IMPRINT",FACE,{"disambiguationData":[TD([[makeQuery(id+"F4.imprint","IMPRINT",EDGE,{"derivedFrom":sQuery(id+"F4.wireOp",EDGE,"E652.0")}),-1.0]])]});
            extrude(context, id + "F5", {"entities" : qUnion([Q0]), "operationType" : NewBodyOperationType.REMOVE, "endBound" : BoundingType.THROUGH_ALL, "oppositeDirection" : true, "depth" : 25 * mm});
        }
    });
